FCSTD DOCUMENT  (FreeCAD 0.19R24276 (Git))
Label: redlizard
Comment: haldis 3d red lizard hotend
License: All rights reserved
LicenseURL: http://en.wikipedia.org/wiki/All_rights_reserved
objects: PartDesign::Plane×33, Sketcher::SketchObject×28, PartDesign::Pocket×24, Part::Helix×19, Part::Part2DObjectPython×15, PartDesign::ShapeBinder×15, PartDesign::Body×11, PartDesign::SubtractivePipe×11, PartDesign::Revolution×4, PartDesign::AdditivePipe×4, PartDesign::FeatureBase×4, PartDesign::Pad×3, PartDesign::SubShapeBinder×2, PartDesign::Groove×1, App::Part×1
note: 221 computed .brp shape members not serialized (recipe doc carries the construction recipe); baked Part::Feature solids carry a one-line shape summary decoded from their .brp

FEATURE [PartDesign::Plane] DatumPlane
  Length = 60
  MapMode = 2
  Placement = pos=(0,0,0) rot=(0.57735,0.57735,0.57735;4.18879rad)
  ResizeMode = 0
  Support = -> [Z_Axis001]
  Width = 60
FEATURE [Sketcher::SketchObject] Sketch
  FullyConstrained = true
  MapMode = 5
  Placement = pos=(0,0,0) rot=(0.57735,0.57735,0.57735;4.18879rad)
  Support = -> [DatumPlane]
  sketch-geometry (9):
    g0: LineSegment StartX=0 StartY=0.2 StartZ=0 EndX=0 EndY=0.5 EndZ=0
    g1: LineSegment StartX=0 StartY=0.5 StartZ=0 EndX=4 EndY=4.45 EndZ=0
    g2: LineSegment StartX=4 StartY=4.45 StartZ=0 EndX=8 EndY=4.45 EndZ=0
    g3: LineSegment StartX=8 StartY=4.45 StartZ=0 EndX=8 EndY=2.5 EndZ=0
    g4: LineSegment StartX=8 StartY=2.5 StartZ=0 EndX=9 EndY=2.5 EndZ=0
    g5: LineSegment StartX=9 StartY=2.5 StartZ=0 EndX=9 EndY=1 EndZ=0
    g6: LineSegment StartX=9 StartY=1 StartZ=0 EndX=1.64252 EndY=1 EndZ=0
    g7: LineSegment StartX=1.64252 StartY=1 StartZ=0 EndX=0.5 EndY=0.2 EndZ=0
    g8: LineSegment StartX=0.5 StartY=0.2 StartZ=0 EndX=0 EndY=0.2 EndZ=0
  constraints (27):
    c: PointOnObject(g0,g-2)
    c: PointOnObject(g0,g-2)
    c: Coincident(g0,g1)
    c: Coincident(g1,g2)
    c: Horizontal(g2)
    c: Coincident(g2,g3)
    c: Vertical(g3)
    c: Coincident(g3,g4)
    c: Horizontal(g4)
    c: Vertical(g5)
    c: Coincident(g5,g6)
    c: Coincident(g6,g7)
    c: Coincident(g7,g8)
    c: Coincident(g8,g0)
    c: Horizontal(g8)
    c: Distance(g-1,g6) = 1
    c: Horizontal(g6)
    c: Distance(g-1,g8) = 0.2
    c: Distance(g0,g-1) = 0.5
    c: Distance(g4) = 1
    c: Distance(g-1,g4) = 2.5
    c: Distance(g-1,g2) = 4.45
    c: Distance(g-1,g3) = 8
    c: Distance(g1,g-2) = 4
    c: Angle(g7,g-1) = 2.53073
    c: Distance(g8) = 0.5
    c: Coincident(g5,g4)
FEATURE [PartDesign::Revolution] Revolution
  Angle = 360
  Axis = (-4e-16,4e-16,1)
  Base = (0,0,0)
  Placement = pos=(0,0,0) rot=(0.57735,0.57735,0.57735;4.18879rad)
  Profile = -> Sketch
  ReferenceAxis = -> Sketch [H_Axis]
FEATURE [PartDesign::Plane] DatumPlane001
  Length = 60
  MapMode = 11
  Placement = pos=(0,0,-1e-16) rot=(0,0,1;1.5708rad)
  ResizeMode = 0
  Support = -> [Revolution]
  Width = 60
FEATURE [Sketcher::SketchObject] Sketch001
  FullyConstrained = true
  MapMode = 5
  Placement = pos=(0,0,-1e-16) rot=(0,0,1;1.5708rad)
  Support = -> [DatumPlane001]
  sketch-geometry (8):
    g0: LineSegment StartX=4 StartY=2.3094 StartZ=0 EndX=7.1e-15 EndY=4.6188 EndZ=0
    g1: LineSegment StartX=7.1e-15 StartY=4.6188 StartZ=0 EndX=-4 EndY=2.3094 EndZ=0
    g2: LineSegment StartX=-4 StartY=2.3094 StartZ=0 EndX=-4 EndY=-2.3094 EndZ=0
    g3: LineSegment StartX=-4 StartY=-2.3094 StartZ=0 EndX=-4.4e-15 EndY=-4.6188 EndZ=0
    g4: LineSegment StartX=-4.4e-15 StartY=-4.6188 StartZ=0 EndX=4 EndY=-2.3094 EndZ=0
    g5: LineSegment StartX=4 StartY=-2.3094 StartZ=0 EndX=4 EndY=2.3094 EndZ=0
    g6: Circle CenterX=0 CenterY=0 CenterZ=0 NormalX=0 NormalY=0 NormalZ=1 AngleXU=0 Radius=4.6188
    g7: Circle CenterX=0 CenterY=0 CenterZ=0 NormalX=0 NormalY=0 NormalZ=1 AngleXU=0 Radius=5
  constraints (18):
    c: Coincident(g0,g1)
    c: Coincident(g1,g2)
    c: Coincident(g2,g3)
    c: Coincident(g3,g4)
    c: Coincident(g4,g5)
    c: Coincident(g5,g0)
    c: Equal(g0, g1-g5) x5
    c: PointOnObject(g0,g6)
    c: PointOnObject(g1,g6)
    c: PointOnObject(g2,g6)
    c: PointOnObject(g3,g6)
    c: PointOnObject(g4,g6)
    c: PointOnObject(g5,g6)
    c: Coincident(g6,g-1)
    c: Perpendicular(g-1,g2)
    c: Distance(g3,g0) = 8
    c: Coincident(g7,g-1)
    c: Radius(g7) = 5
FEATURE [PartDesign::Pocket] Pocket
  BaseFeature = -> Revolution
  Length = 5
  Length2 = 100
  Placement = pos=(0,0,0) rot=(0.57735,0.57735,0.57735;4.18879rad)
  Profile = -> Sketch001
  Reversed = true
  Type = 1
FEATURE [PartDesign::Plane] DatumPlane003
  Length = 81.2898
  MapMode = 2
  Placement = pos=(0,0,0) rot=(0.57735,0.57735,0.57735;4.18879rad)
  ResizeMode = 0
  Support = -> [Z_Axis002]
  Width = 61.7898
FEATURE [PartDesign::Plane] DatumPlane004
  AttachmentOffset = pos=(0,0,-18.5) rot=(0,0,1;0rad)
  Length = 60
  MapMode = 5
  Placement = pos=(0,0,18.5) rot=(0,1,0;3.14159rad)
  ResizeMode = 0
  Support = -> [XY_Plane003]
  Width = 60
FEATURE [Sketcher::SketchObject] Sketch004
  FullyConstrained = true
  MapMode = 5
  Placement = pos=(0,0,18.5) rot=(0,1,0;3.14159rad)
  Support = -> [DatumPlane004]
  sketch-geometry (7):
    g0: LineSegment StartX=-10 StartY=6 StartZ=0 EndX=10 EndY=6 EndZ=0
    g1: LineSegment StartX=10 StartY=6 StartZ=0 EndX=10 EndY=-14 EndZ=0
    g2: LineSegment StartX=10 StartY=-14 StartZ=0 EndX=-10 EndY=-14 EndZ=0
    g3: LineSegment StartX=-10 StartY=-14 StartZ=0 EndX=-10 EndY=6 EndZ=0
    g4: Circle CenterX=-8 CenterY=0 CenterZ=0 NormalX=0 NormalY=0 NormalZ=1 AngleXU=0 Radius=0.8
    g5: Circle CenterX=8 CenterY=0 CenterZ=0 NormalX=0 NormalY=0 NormalZ=1 AngleXU=0 Radius=0.8
    g6: Circle CenterX=0 CenterY=0 CenterZ=0 NormalX=0 NormalY=0 NormalZ=1 AngleXU=0 Radius=2.3
  constraints (18):
    c: Coincident(g0,g1)
    c: Coincident(g1,g2)
    c: Coincident(g2,g3)
    c: Coincident(g3,g0)
    c: Horizontal(g2)
    c: Vertical(g1)
    c: Vertical(g3)
    c: Equal(g0,g1)
    c: Symmetric(g0,g0,g-2)
    c: Distance(g0,g-1) = 6
    c: Distance(g0) = 20
    c: PointOnObject(g4,g-1)
    c: Equal(g4,g5)
    c: Symmetric(g5,g4,g-1)
    c: Radius(g5) = 0.8
    c: Distance(g5,g4) = 16
    c: Coincident(g6,g-1)
    c: Radius(g6) = 2.3
FEATURE [PartDesign::Pad] Pad
  Direction = (1,1,1)
  Length = 10
  Length2 = 100
  Placement = pos=(0,0,18.5) rot=(0,1,0;3.14159rad)
  Profile = -> Sketch004
  Type = 0
FEATURE [PartDesign::Plane] DatumPlane005
  Length = 60
  MapMode = 5
  Placement = pos=(10,0,18.5) rot=(0.57735,-0.57735,0.57735;4.18879rad)
  ResizeMode = 0
  Support = -> [Pad]
  Width = 60
FEATURE [Sketcher::SketchObject] Sketch005
  FullyConstrained = true
  MapMode = 5
  Placement = pos=(10,0,18.5) rot=(-0.57735,0.57735,-0.57735;2.0944rad)
  Support = -> [DatumPlane005]
  sketch-geometry (6):
    g0: Circle CenterX=9.9 CenterY=5.5 CenterZ=0 NormalX=0 NormalY=0 NormalZ=1 AngleXU=0 Radius=3.1
    g1: Circle CenterX=6 CenterY=2.2 CenterZ=0 NormalX=0 NormalY=0 NormalZ=1 AngleXU=0 Radius=1.55
    g2: Circle CenterX=3 CenterY=4.5 CenterZ=0 NormalX=0 NormalY=0 NormalZ=1 AngleXU=0 Radius=1.18
    g3: Circle CenterX=3 CenterY=8 CenterZ=0 NormalX=0 NormalY=0 NormalZ=1 AngleXU=0 Radius=1
    g4: LineSegment StartX=3 StartY=10 StartZ=0 EndX=3 EndY=6 EndZ=0
    g5: Circle CenterX=3 CenterY=4.5 CenterZ=0 NormalX=0 NormalY=0 NormalZ=1 AngleXU=0 Radius=1.5
  constraints (17):
    c: Radius(g0) = 3.1
    c: Radius(g3) = 1
    c: Radius(g2) = 1.18
    c: Radius(g1) = 1.55
    c: Distance(g1,g-1) = 2.2
    c: Distance(g2,g-1) = 4.5
    c: Vertical(g3,g2)
    c: Vertical(g4)
    c: Symmetric(g4,g4,g3)
    c: Coincident(g5,g2)
    c: Radius(g5) = 1.5
    c: PointOnObject(g4,g5)
    c: DistanceX(g0) = 9.9
    c: DistanceY(g0) = 5.5
    c: DistanceX(g1) = 6
    c: DistanceX(g2) = 3
    c: DistanceY(g4) = 10
FEATURE [PartDesign::Pocket] Pocket002
  BaseFeature = -> Pad
  Length = 5
  Length2 = 100
  Placement = pos=(0,0,18.5) rot=(0,1,0;3.14159rad)
  Profile = -> Sketch005
  Type = 0
FEATURE [PartDesign::Plane] DatumPlane006
  Length = 60
  MapMode = 5
  Placement = pos=(0,0,18.5) rot=(0,0,1;3.14159rad)
  ResizeMode = 0
  Support = -> [Pocket002]
  Width = 60
FEATURE [Sketcher::SketchObject] Sketch006
  FullyConstrained = true
  MapMode = 5
  Placement = pos=(0,0,18.5) rot=(0,0,1;3.14159rad)
  Support = -> [DatumPlane006]
  sketch-geometry (1):
    g0: Circle CenterX=0 CenterY=9.9 CenterZ=0 NormalX=0 NormalY=0 NormalZ=1 AngleXU=0 Radius=1.18
  constraints (3):
    c: PointOnObject(g0,g-2)
    c: Radius(g0) = 1.18
    c: Distance(g0,g-1) = 9.9
FEATURE [PartDesign::Pocket] Pocket006
  BaseFeature = -> Pocket002
  Length = 5
  Length2 = 100
  Placement = pos=(0,0,18.5) rot=(0,1,0;3.14159rad)
  Profile = -> Sketch006
  Type = 0
FEATURE [PartDesign::Plane] DatumPlane007
  Length = 60
  MapMode = 5
  Placement = pos=(-3.7e-15,0,8.5) rot=(0,1,0;3.14159rad)
  ResizeMode = 0
  Support = -> [Pocket006]
  Width = 60
FEATURE [Sketcher::SketchObject] Sketch007
  FullyConstrained = true
  MapMode = 5
  Placement = pos=(-3.7e-15,0,8.5) rot=(0,1,0;3.14159rad)
  Support = -> [DatumPlane007]
  sketch-geometry (1):
    g0: Circle CenterX=4 CenterY=-5 CenterZ=0 NormalX=0 NormalY=0 NormalZ=1 AngleXU=0 Radius=1.18
  constraints (3):
    c: Radius(g0) = 1.18
    c: Distance(g0,g-2) = 4
    c: Distance(g0,g-1) = 5
FEATURE [PartDesign::Pocket] Pocket007
  BaseFeature = -> Pocket006
  Length = 7
  Length2 = 100
  Placement = pos=(0,0,18.5) rot=(0,1,0;3.14159rad)
  Profile = -> Sketch007
  Type = 0
FEATURE [Sketcher::SketchObject] Sketch008
  ExternalGeometry = -> [Pocket007]
  FullyConstrained = true
  MapMode = 5
  Placement = pos=(0,0,18.5) rot=(0,1,0;3.14159rad)
  Support = -> [DatumPlane004]
  sketch-geometry (4):
    g0: Circle CenterX=-6 CenterY=3 CenterZ=0 NormalX=0 NormalY=0 NormalZ=1 AngleXU=0 Radius=1
    g1: Circle CenterX=-6 CenterY=-3 CenterZ=0 NormalX=0 NormalY=0 NormalZ=1 AngleXU=0 Radius=1
    g2: Circle CenterX=6 CenterY=3 CenterZ=0 NormalX=0 NormalY=0 NormalZ=1 AngleXU=0 Radius=1
    g3: Circle CenterX=6 CenterY=-3 CenterZ=0 NormalX=0 NormalY=0 NormalZ=1 AngleXU=0 Radius=1
  constraints (10):
    c: Equal(g3,g2)
    c: Equal(g2,g0)
    c: Equal(g0,g1)
    c: Horizontal(g1,g3)
    c: Vertical(g2,g3)
    c: Symmetric(g0,g2,g-2)
    c: Symmetric(g1,g0,g-1)
    c: Distance(g0,g1) = 6
    c: Distance(g2,g0) = 12
    c: Radius(g2) = 1
FEATURE [PartDesign::Pocket] Pocket008
  BaseFeature = -> Pocket007
  Length = 2.5
  Length2 = 100
  Placement = pos=(0,0,18.5) rot=(0,1,0;3.14159rad)
  Profile = -> Sketch008
  Reversed = true
  Type = 0
FEATURE [PartDesign::Plane] DatumPlane010
  Length = 93.1886
  MapMode = 2
  Placement = pos=(0,0,0) rot=(0.57735,0.57735,0.57735;4.18879rad)
  ResizeMode = 0
  Support = -> [Z_Axis004]
  Width = 62.6886
FEATURE [Sketcher::SketchObject] Sketch009
  FullyConstrained = true
  MapMode = 5
  Placement = pos=(0,0,0) rot=(0.57735,0.57735,0.57735;4.18879rad)
  Support = -> [DatumPlane010]
  sketch-geometry (71):
    g0: LineSegment StartX=23.5 StartY=0 StartZ=0 EndX=23.5 EndY=10.5 EndZ=0
    g1: LineSegment StartX=55.5 StartY=10.5 StartZ=0 EndX=55.5 EndY=0 EndZ=0
    g2: LineSegment StartX=55.5 StartY=0 StartZ=0 EndX=23.5 EndY=0 EndZ=0
    g3: LineSegment StartX=23.5 StartY=10.5 StartZ=0 EndX=26.5 EndY=10.5 EndZ=0
    g4: LineSegment StartX=55.5 StartY=10.5 StartZ=0 EndX=43.5 EndY=10.5 EndZ=0
    g5: LineSegment StartX=23.5 StartY=8.5 StartZ=0 EndX=55.5 EndY=8.5 EndZ=0
    g6: LineSegment StartX=23.5 StartY=8.3 StartZ=0 EndX=55.5 EndY=8.3 EndZ=0
    g7: LineSegment StartX=26.5 StartY=10.5 StartZ=0 EndX=26.5 EndY=8.5 EndZ=0
    g8: LineSegment StartX=26.5 StartY=8.5 StartZ=0 EndX=27.5 EndY=8.5 EndZ=0
    g9: LineSegment StartX=43.5 StartY=10.5 StartZ=0 EndX=43.5 EndY=8.5 EndZ=0
    g10: LineSegment StartX=43.5 StartY=8.5 StartZ=0 EndX=42.5 EndY=8.5 EndZ=0
    g11: LineSegment StartX=27.5 StartY=8.5 StartZ=0 EndX=27.5 EndY=10.5 EndZ=0
    g12: LineSegment StartX=27.5 StartY=10.5 StartZ=0 EndX=28.2778 EndY=10.5 EndZ=0
    g13: LineSegment StartX=28.2778 StartY=10.5 StartZ=0 EndX=28.2778 EndY=7.3 EndZ=0
    g14: LineSegment StartX=28.2778 StartY=7.3 StartZ=0 EndX=29.2778 EndY=7.3 EndZ=0
    g15: LineSegment StartX=29.2778 StartY=7.3 StartZ=0 EndX=29.2778 EndY=10.5 EndZ=0
    g16: LineSegment StartX=29.2778 StartY=10.5 StartZ=0 EndX=30.0556 EndY=10.5 EndZ=0
    g17: LineSegment StartX=30.0556 StartY=10.5 StartZ=0 EndX=30.0556 EndY=7.3 EndZ=0
    g18: LineSegment StartX=30.0556 StartY=7.3 StartZ=0 EndX=31.0556 EndY=7.3 EndZ=0
    g19: LineSegment StartX=31.0556 StartY=7.3 StartZ=0 EndX=31.0556 EndY=10.5 EndZ=0
    g20: LineSegment StartX=31.0556 StartY=10.5 StartZ=0 EndX=31.8333 EndY=10.5 EndZ=0
    g21: LineSegment StartX=31.8333 StartY=10.5 StartZ=0 EndX=31.8333 EndY=7.3 EndZ=0
    g22: LineSegment StartX=31.8333 StartY=7.3 StartZ=0 EndX=32.8333 EndY=7.3 EndZ=0
    g23: LineSegment StartX=32.8333 StartY=7.3 StartZ=0 EndX=32.8333 EndY=10.5 EndZ=0
    g24: LineSegment StartX=32.8333 StartY=10.5 StartZ=0 EndX=33.6111 EndY=10.5 EndZ=0
    g25: LineSegment StartX=33.6111 StartY=10.5 StartZ=0 EndX=33.6111 EndY=7.3 EndZ=0
    g26: LineSegment StartX=33.6111 StartY=7.3 StartZ=0 EndX=34.6111 EndY=7.3 EndZ=0
    g27: LineSegment StartX=34.6111 StartY=7.3 StartZ=0 EndX=34.6111 EndY=10.5 EndZ=0
    g28: LineSegment StartX=34.6111 StartY=10.5 StartZ=0 EndX=35.3889 EndY=10.5 EndZ=0
    g29: LineSegment StartX=35.3889 StartY=10.5 StartZ=0 EndX=35.3889 EndY=7.3 EndZ=0
    g30: LineSegment StartX=35.3889 StartY=7.3 StartZ=0 EndX=36.3889 EndY=7.3 EndZ=0
    g31: LineSegment StartX=36.3889 StartY=7.3 StartZ=0 EndX=36.3889 EndY=10.5 EndZ=0
    g32: LineSegment StartX=36.3889 StartY=10.5 StartZ=0 EndX=37.1667 EndY=10.5 EndZ=0
    g33: LineSegment StartX=37.1667 StartY=10.5 StartZ=0 EndX=37.1667 EndY=7.3 EndZ=0
    g34: LineSegment StartX=37.1667 StartY=7.3 StartZ=0 EndX=38.1667 EndY=7.3 EndZ=0
    g35: LineSegment StartX=38.1667 StartY=7.3 StartZ=0 EndX=38.1667 EndY=10.5 EndZ=0
    g36: LineSegment StartX=38.1667 StartY=10.5 StartZ=0 EndX=38.9444 EndY=10.5 EndZ=0
    g37: LineSegment StartX=38.9444 StartY=10.5 StartZ=0 EndX=38.9444 EndY=7.3 EndZ=0
    g38: LineSegment StartX=38.9444 StartY=7.3 StartZ=0 EndX=39.9444 EndY=7.3 EndZ=0
    g39: LineSegment StartX=39.9444 StartY=7.3 StartZ=0 EndX=39.9444 EndY=10.5 EndZ=0
    g40: LineSegment StartX=39.9444 StartY=10.5 StartZ=0 EndX=40.7222 EndY=10.5 EndZ=0
    g41: LineSegment StartX=40.7222 StartY=10.5 StartZ=0 EndX=40.7222 EndY=7.3 EndZ=0
    g42: LineSegment StartX=40.7222 StartY=7.3 StartZ=0 EndX=41.7222 EndY=7.3 EndZ=0
    g43: LineSegment StartX=41.7222 StartY=7.3 StartZ=0 EndX=41.7222 EndY=10.5 EndZ=0
    g44: LineSegment StartX=41.7222 StartY=10.5 StartZ=0 EndX=42.5 EndY=10.5 EndZ=0
    g45: LineSegment StartX=42.5 StartY=10.5 StartZ=0 EndX=42.5 EndY=8.5 EndZ=0
    g46: ArcOfCircle CenterX=35 CenterY=121.371 CenterZ=0 NormalX=0 NormalY=0 NormalZ=1 AngleXU=0 Radius=113.071 StartAngle=4.6529 EndAngle=4.77188
    g47: ArcOfCircle CenterX=35 CenterY=121.371 CenterZ=0 NormalX=0 NormalY=0 NormalZ=1 AngleXU=0 Radius=113.071 StartAngle=4.6529 EndAngle=4.66176
    g48: LineSegment StartX=28.2778 StartY=10.5 StartZ=0 EndX=28.2778 EndY=8.5 EndZ=0
    g49: LineSegment StartX=29.2778 StartY=10.5 StartZ=0 EndX=29.2778 EndY=8.44489 EndZ=0
    g50: LineSegment StartX=30.0556 StartY=10.5 StartZ=0 EndX=30.0556 EndY=8.40816 EndZ=0
    g51: LineSegment StartX=31.0556 StartY=10.5 StartZ=0 EndX=31.0556 EndY=8.36882 EndZ=0
    g52: LineSegment StartX=31.8333 StartY=10.5 StartZ=0 EndX=31.8333 EndY=8.34435 EndZ=0
    g53: LineSegment StartX=32.8333 StartY=10.5 StartZ=0 EndX=32.8333 EndY=8.32076 EndZ=0
    g54: LineSegment StartX=33.6111 StartY=10.5 StartZ=0 EndX=33.6111 EndY=8.30853 EndZ=0
    g55: LineSegment StartX=34.6111 StartY=10.5 StartZ=0 EndX=34.6111 EndY=8.30067 EndZ=0
    g56: LineSegment StartX=35.3889 StartY=10.5 StartZ=0 EndX=35.3889 EndY=8.30067 EndZ=0
    g57: LineSegment StartX=36.3889 StartY=10.5 StartZ=0 EndX=36.3889 EndY=8.30853 EndZ=0
    g58: LineSegment StartX=37.1667 StartY=10.5 StartZ=0 EndX=37.1667 EndY=8.32076 EndZ=0
    g59: LineSegment StartX=38.1667 StartY=10.5 StartZ=0 EndX=38.1667 EndY=8.34435 EndZ=0
    g60: LineSegment StartX=38.9444 StartY=10.5 StartZ=0 EndX=38.9444 EndY=8.36882 EndZ=0
    g61: LineSegment StartX=39.9444 StartY=10.5 StartZ=0 EndX=39.9444 EndY=8.40816 EndZ=0
    g62: LineSegment StartX=40.7222 StartY=10.5 StartZ=0 EndX=40.7222 EndY=8.44489 EndZ=0
    g63: LineSegment StartX=41.7222 StartY=10.5 StartZ=0 EndX=41.7222 EndY=8.5 EndZ=0
    g64: ArcOfCircle CenterX=35 CenterY=121.371 CenterZ=0 NormalX=0 NormalY=0 NormalZ=1 AngleXU=0 Radius=113.071 StartAngle=4.76302 EndAngle=4.77188
    g65: ArcOfCircle CenterX=35 CenterY=121.371 CenterZ=0 NormalX=0 NormalY=0 NormalZ=1 AngleXU=0 Radius=113.071 StartAngle=4.74728 EndAngle=4.75613
    g66: ArcOfCircle CenterX=35 CenterY=121.371 CenterZ=0 NormalX=0 NormalY=0 NormalZ=1 AngleXU=0 Radius=113.071 StartAngle=4.73155 EndAngle=4.7404
    g67: ArcOfCircle CenterX=35 CenterY=121.371 CenterZ=0 NormalX=0 NormalY=0 NormalZ=1 AngleXU=0 Radius=113.071 StartAngle=4.71583 EndAngle=4.72467
    g68: ArcOfCircle CenterX=35 CenterY=121.371 CenterZ=0 NormalX=0 NormalY=0 NormalZ=1 AngleXU=0 Radius=113.071 StartAngle=4.70011 EndAngle=4.70895
    g69: ArcOfCircle CenterX=35 CenterY=121.371 CenterZ=0 NormalX=0 NormalY=0 NormalZ=1 AngleXU=0 Radius=113.071 StartAngle=4.68438 EndAngle=4.69323
    g70: ArcOfCircle CenterX=35 CenterY=121.371 CenterZ=0 NormalX=0 NormalY=0 NormalZ=1 AngleXU=0 Radius=113.071 StartAngle=4.66865 EndAngle=4.6775
  constraints (222):
    c: PointOnObject(g0,g-1)
    c: Vertical(g0)
    c: PointOnObject(g1,g-1)
    c: Vertical(g1)
    c: Coincident(g1,g2)
    c: Coincident(g2,g0)
    c: Distance(g1) = 10.5
    c: Distance(g2) = 32
    c: Coincident(g3,g0)
    c: Horizontal(g3)
    c: Coincident(g4,g1)
    c: Horizontal(g4)
    c: Distance(g4) = 12
    c: Distance(g3) = 3
    c: Horizontal(g0,g1)
    c: PointOnObject(g5,g1)
    c: Horizontal(g5)
    c: PointOnObject(g5,g0)
    c: Distance(g3,g5) = 2
    c: PointOnObject(g6,g0)
    c: PointOnObject(g6,g1)
    c: Horizontal(g6)
    c: Distance(g3,g6) = 2.2
    c: Coincident(g7,g3)
    c: PointOnObject(g7,g5)
    c: Vertical(g7)
    c: Coincident(g8,g7)
    c: PointOnObject(g8,g5)
    c: Coincident(g9,g4)
    c: PointOnObject(g9,g5)
    c: Vertical(g9)
    c: Coincident(g10,g9)
    c: PointOnObject(g10,g5)
    c: Equal(g8,g10)
    c: Distance(g8) = 1
    c: Coincident(g8,g11)
    c: Vertical(g11)
    c: Coincident(g11,g12)
    c: Horizontal(g12)
    c: Coincident(g12,g13)
    c: Vertical(g13)
    c: Coincident(g13,g14)
    c: Horizontal(g14)
    c: Coincident(g14,g15)
    c: Vertical(g15)
    c: Coincident(g15,g16)
    c: Horizontal(g16)
    c: Coincident(g16,g17)
    c: Vertical(g17)
    c: Coincident(g17,g18)
    c: Horizontal(g18)
    c: Coincident(g18,g19)
    c: Vertical(g19)
    c: Coincident(g19,g20)
    c: Horizontal(g20)
    c: Coincident(g20,g21)
    c: Vertical(g21)
    c: Coincident(g21,g22)
    c: Horizontal(g22)
    c: Coincident(g22,g23)
    c: Vertical(g23)
    c: Coincident(g23,g24)
    c: Horizontal(g24)
    c: Coincident(g24,g25)
    c: Vertical(g25)
    c: Coincident(g25,g26)
    c: Horizontal(g26)
    c: Coincident(g26,g27)
    c: Vertical(g27)
    c: Coincident(g27,g28)
    c: Horizontal(g28)
    c: Coincident(g28,g29)
    c: Vertical(g29)
    c: Coincident(g29,g30)
    c: Horizontal(g30)
    c: Coincident(g30,g31)
    c: Vertical(g31)
    c: Coincident(g31,g32)
    c: Horizontal(g32)
    c: Coincident(g32,g33)
    c: Vertical(g33)
    c: Coincident(g33,g34)
    c: Horizontal(g34)
    c: Coincident(g34,g35)
    c: Vertical(g35)
    c: Coincident(g35,g36)
    c: Horizontal(g36)
    c: Coincident(g36,g37)
    c: Vertical(g37)
    c: Coincident(g37,g38)
    c: Horizontal(g38)
    c: Coincident(g38,g39)
    c: Vertical(g39)
    c: Coincident(g39,g40)
    c: Horizontal(g40)
    c: Coincident(g40,g41)
    c: Vertical(g41)
    c: Coincident(g41,g42)
    c: Horizontal(g42)
    c: Coincident(g42,g43)
    c: Vertical(g43)
    c: Coincident(g43,g44)
    c: Horizontal(g44)
    c: Coincident(g44,g45)
    c: Coincident(g45,g10)
    c: Vertical(g45)
    c: Horizontal(g3,g12)
    c: Horizontal(g12,g16)
    c: Horizontal(g16,g20)
    c: Horizontal(g20,g24)
    c: Horizontal(g24,g28)
    c: Horizontal(g28,g32)
    c: Horizontal(g32,g36)
    c: Horizontal(g36,g40)
    c: Horizontal(g40,g44)
    c: Equal(g8,g14)
    c: Equal(g14,g18)
    c: Equal(g18,g22)
    c: Equal(g22,g26)
    c: Equal(g26,g30)
    c: Equal(g30,g34)
    c: Equal(g34,g38)
    c: Equal(g38,g42)
    c: Equal(g12,g16)
    c: Equal(g16,g20)
    c: Equal(g20,g24)
    c: Equal(g24,g28)
    c: Equal(g28,g32)
    c: Equal(g32,g36)
    c: Equal(g36,g40)
    c: Equal(g40,g44)
    c: PointOnObject(g46,g13)
    c: PointOnObject(g46,g43)
    c: PointOnObject(g46,g5)
    c: PointOnObject(g46,g5)
    c: Tangent(g46,g6)
    c: Coincident(g47,g46)
    c: Coincident(g47,g46)
    c: Coincident(g64,g46)
    c: Coincident(g48,g12)
    c: Coincident(g48,g47)
    c: Vertical(g48)
    c: Coincident(g49,g16)
    c: PointOnObject(g49,g47)
    c: Vertical(g49)
    c: Coincident(g50,g16)
    c: PointOnObject(g50,g47)
    c: Vertical(g50)
    c: Coincident(g51,g20)
    c: PointOnObject(g51,g47)
    c: Vertical(g51)
    c: Coincident(g52,g20)
    c: PointOnObject(g52,g47)
    c: Vertical(g52)
    c: Coincident(g53,g24)
    c: PointOnObject(g53,g47)
    c: Vertical(g53)
    c: Coincident(g54,g24)
    c: PointOnObject(g54,g47)
    c: Vertical(g54)
    c: Coincident(g55,g28)
    c: PointOnObject(g55,g47)
    c: Vertical(g55)
    c: Coincident(g56,g28)
    c: PointOnObject(g56,g47)
    c: Vertical(g56)
    c: Coincident(g57,g32)
    c: PointOnObject(g57,g47)
    c: Vertical(g57)
    c: Coincident(g58,g32)
    c: PointOnObject(g58,g47)
    c: Vertical(g58)
    c: Coincident(g59,g36)
    c: Vertical(g59)
    c: Coincident(g60,g36)
    c: PointOnObject(g60,g47)
    c: Vertical(g60)
    c: Coincident(g61,g40)
    c: PointOnObject(g61,g47)
    c: Vertical(g61)
    c: Coincident(g62,g40)
    c: PointOnObject(g62,g47)
    c: Vertical(g62)
    c: Coincident(g63,g44)
    c: PointOnObject(g63,g47)
    c: Vertical(g63)
    c: Equal(g47,g64)
    c: PointOnObject(g65,g39)
    c: PointOnObject(g64,g41)
    c: Coincident(g47,g64)
    c: Equal(g47,g65)
    c: Coincident(g66,g59)
    c: PointOnObject(g65,g37)
    c: Coincident(g47,g65)
    c: Equal(g47,g66)
    c: PointOnObject(g67,g31)
    c: PointOnObject(g66,g33)
    c: Coincident(g47,g66)
    c: PointOnObject(g68,g27)
    c: Coincident(g47,g67)
    c: Equal(g47,g68)
    c: PointOnObject(g69,g23)
    c: PointOnObject(g68,g25)
    c: Coincident(g47,g68)
    c: Equal(g47,g69)
    c: PointOnObject(g70,g19)
    c: PointOnObject(g69,g21)
    c: Coincident(g47,g69)
    c: Equal(g47,g70)
    c: PointOnObject(g47,g15)
    c: PointOnObject(g70,g17)
    c: Coincident(g47,g70)
    c: Coincident(g67,g56)
    c: Horizontal(g14,g18)
    c: Horizontal(g18,g22)
    c: Horizontal(g22,g26)
    c: Horizontal(g26,g30)
    c: Horizontal(g30,g34)
    c: Horizontal(g34,g38)
    c: Horizontal(g38,g42)
    c: Distance(g42,g6) = 1
    c: Distance(g0,g-2) = 23.5
FEATURE [PartDesign::Revolution] Revolution002
  Angle = 360
  Axis = (-4e-16,4e-16,1)
  Base = (0,0,0)
  Placement = pos=(0,0,0) rot=(0.57735,0.57735,0.57735;4.18879rad)
  Profile = -> Sketch009
  ReferenceAxis = -> Sketch009 [H_Axis]
FEATURE [PartDesign::Plane] DatumPlane011
  Length = 62.6886
  MapMode = 5
  Placement = pos=(0,0,0) rot=(0.57735,0.57735,0.57735;2.0944rad)
  ResizeMode = 0
  Support = -> [YZ_Plane004]
  Width = 93.1886
FEATURE [Sketcher::SketchObject] Sketch010
  ExternalGeometry = -> [Revolution002]
  FullyConstrained = true
  MapMode = 5
  Placement = pos=(0,0,0) rot=(0.57735,0.57735,0.57735;2.0944rad)
  Support = -> [DatumPlane011]
  sketch-geometry (9):
    g0: LineSegment StartX=-6 StartY=55.5 StartZ=0 EndX=6 EndY=55.5 EndZ=0
    g1: LineSegment StartX=6 StartY=55.5 StartZ=0 EndX=6 EndY=23.5 EndZ=0
    g2: LineSegment StartX=6 StartY=23.5 StartZ=0 EndX=-6 EndY=23.5 EndZ=0
    g3: LineSegment StartX=-6 StartY=23.5 StartZ=0 EndX=-6 EndY=55.5 EndZ=0
    g4: LineSegment StartX=-12.5 StartY=58.5476 StartZ=0 EndX=12.5 EndY=58.5476 EndZ=0
    g5: LineSegment StartX=12.5 StartY=58.5476 StartZ=0 EndX=12.5 EndY=20.4524 EndZ=0
    g6: LineSegment StartX=12.5 StartY=20.4524 StartZ=0 EndX=-12.5 EndY=20.4524 EndZ=0
    g7: LineSegment StartX=-12.5 StartY=20.4524 StartZ=0 EndX=-12.5 EndY=58.5476 EndZ=0
    g8: LineSegment StartX=12.5 StartY=58.5476 StartZ=0 EndX=-12.5 EndY=20.4524 EndZ=0
  constraints (24):
    c: Coincident(g0,g1)
    c: Coincident(g1,g2)
    c: Coincident(g2,g3)
    c: Coincident(g3,g0)
    c: Horizontal(g2)
    c: Vertical(g1)
    c: Vertical(g3)
    c: PointOnObject(g0,g-3)
    c: PointOnObject(g1,g-4)
    c: Symmetric(g0,g0,g-2)
    c: Distance(g0) = 12
    c: Coincident(g4,g5)
    c: Coincident(g5,g6)
    c: Coincident(g6,g7)
    c: Coincident(g7,g4)
    c: Horizontal(g6)
    c: Vertical(g5)
    c: Vertical(g7)
    c: Symmetric(g4,g4,g-2)
    c: Distance(g6) = 25
    c: Coincident(g8,g4)
    c: Coincident(g8,g6)
    c: PointOnObject(g-4,g8)
    c: PointOnObject(g-3,g8)
FEATURE [PartDesign::Pocket] Pocket010
  BaseFeature = -> Revolution002
  Length = 5
  Length2 = 100
  Midplane = true
  Placement = pos=(0,0,0) rot=(0.57735,0.57735,0.57735;4.18879rad)
  Profile = -> Sketch010
  Type = 1
FEATURE [PartDesign::Plane] DatumPlane012
  Length = 62.6886
  MapMode = 5
  Placement = pos=(0,0,0) rot=(1,0,0;1.5708rad)
  ResizeMode = 0
  Support = -> [XZ_Plane004]
  Width = 93.1886
FEATURE [Sketcher::SketchObject] Sketch011
  ExternalGeometry = -> [Pocket010]
  FullyConstrained = true
  MapMode = 5
  Placement = pos=(0,0,0) rot=(1,0,0;1.5708rad)
  Support = -> [DatumPlane012]
  sketch-geometry (8):
    g0: LineSegment StartX=-5.25 StartY=42.5 StartZ=0 EndX=5.25 EndY=42.5 EndZ=0
    g1: LineSegment StartX=6.25 StartY=41.5 StartZ=0 EndX=6.25 EndY=27.5 EndZ=0
    g2: LineSegment StartX=5.25 StartY=26.5 StartZ=0 EndX=-5.25 EndY=26.5 EndZ=0
    g3: LineSegment StartX=-6.25 StartY=27.5 StartZ=0 EndX=-6.25 EndY=41.5 EndZ=0
    g4: ArcOfCircle CenterX=-5.25 CenterY=41.5 CenterZ=0 NormalX=0 NormalY=0 NormalZ=1 AngleXU=0 Radius=1 StartAngle=1.5708 EndAngle=3.14159
    g5: ArcOfCircle CenterX=5.25 CenterY=41.5 CenterZ=0 NormalX=0 NormalY=0 NormalZ=1 AngleXU=0 Radius=1 StartAngle=-9e-16 EndAngle=1.5708
    g6: ArcOfCircle CenterX=5.25 CenterY=27.5 CenterZ=0 NormalX=0 NormalY=0 NormalZ=1 AngleXU=0 Radius=1 StartAngle=4.71239 EndAngle=6.28319
    g7: ArcOfCircle CenterX=-5.25 CenterY=27.5 CenterZ=0 NormalX=0 NormalY=0 NormalZ=1 AngleXU=0 Radius=1 StartAngle=3.14159 EndAngle=4.71239
  constraints (19):
    c: Horizontal(g0)
    c: Horizontal(g2)
    c: Vertical(g1)
    c: Vertical(g3)
    c: Tangent(g3,g4) = 1.5708
    c: Tangent(g0,g4) = 1.5708
    c: Tangent(g0,g5) = 1.5708
    c: Tangent(g1,g5) = 1.5708
    c: Tangent(g1,g6) = 1.5708
    c: Tangent(g2,g6) = 1.5708
    c: Tangent(g2,g7) = 1.5708
    c: Tangent(g3,g7) = 1.5708
    c: Radius(g6) = 1
    c: Equal(g6,g7)
    c: Equal(g6,g4)
    c: Distance(g3,g1) = 12.5
    c: Distance(g0,g2) = 16
    c: Symmetric(g5,g4,g-2)
    c: Distance(g-1,g2) = 26.5
FEATURE [PartDesign::Pocket] Pocket011
  BaseFeature = -> Pocket010
  Length = 5
  Length2 = 100
  Midplane = true
  Placement = pos=(0,0,0) rot=(0.57735,0.57735,0.57735;4.18879rad)
  Profile = -> Sketch011
  Type = 1
FEATURE [PartDesign::Plane] DatumPlane013
  Length = 62.6886
  MapMode = 5
  Placement = pos=(0,0,0) rot=(0.57735,0.57735,0.57735;2.0944rad)
  ResizeMode = 0
  Support = -> [YZ_Plane004]
  Width = 93.1886
FEATURE [Sketcher::SketchObject] Sketch012
  ExternalGeometry = -> [Pocket011]
  FullyConstrained = true
  MapMode = 5
  Placement = pos=(0,0,0) rot=(0.57735,0.57735,0.57735;2.0944rad)
  Support = -> [DatumPlane013]
  sketch-geometry (6):
    g0: ArcOfCircle CenterX=0 CenterY=39 CenterZ=0 NormalX=0 NormalY=0 NormalZ=1 AngleXU=0 Radius=2.5 StartAngle=-9e-16 EndAngle=3.14159
    g1: ArcOfCircle CenterX=1e-16 CenterY=31 CenterZ=0 NormalX=0 NormalY=0 NormalZ=1 AngleXU=0 Radius=2.5 StartAngle=3.14159 EndAngle=6.28319
    g2: LineSegment StartX=-2.5 StartY=39 StartZ=0 EndX=-2.5 EndY=31 EndZ=0
    g3: LineSegment StartX=2.5 StartY=39 StartZ=0 EndX=2.5 EndY=31 EndZ=0
    g4: LineSegment StartX=0 StartY=41.7222 StartZ=0 EndX=0 EndY=28.2778 EndZ=0
    g5: LineSegment StartX=-2.5 StartY=35 StartZ=0 EndX=2.5 EndY=35 EndZ=0
  constraints (16):
    c: Tangent(g0,g3) = 1.5708
    c: Tangent(g0,g2) = -1.5708
    c: Tangent(g2,g1) = -1.5708
    c: Tangent(g3,g1) = 1.5708
    c: Vertical(g2)
    c: Equal(g0,g1)
    c: Radius(g0) = 2.5
    c: Distance(g0,g1) = 8
    c: PointOnObject(g0,g-2)
    c: Vertical(g4)
    c: PointOnObject(g4,g-2)
    c: PointOnObject(g5,g2)
    c: Symmetric(g0,g1,g5)
    c: Symmetric(g4,g4,g5)
    c: PointOnObject(g4,g-4)
    c: PointOnObject(g4,g-3)
FEATURE [PartDesign::Pocket] Pocket012
  BaseFeature = -> Pocket011
  Length = 5
  Length2 = 100
  Midplane = true
  Placement = pos=(0,0,0) rot=(0.57735,0.57735,0.57735;4.18879rad)
  Profile = -> Sketch012
  Type = 1
FEATURE [PartDesign::Plane] DatumPlane014
  Length = 60
  MapMode = 5
  Placement = pos=(5.9e-15,-1.47e-14,26.5) rot=(0,0,1;0rad)
  ResizeMode = 0
  Support = -> [Pocket012]
  Width = 60
FEATURE [Sketcher::SketchObject] Sketch013
  FullyConstrained = true
  MapMode = 5
  Placement = pos=(5.9e-15,-1.47e-14,26.5) rot=(0,0,1;0rad)
  Support = -> [DatumPlane014]
  sketch-geometry (1):
    g0: Circle CenterX=0 CenterY=0 CenterZ=0 NormalX=0 NormalY=0 NormalZ=1 AngleXU=0 Radius=5
  constraints (2):
    c: Coincident(g0,g-1)
    c: Radius(g0) = 5
FEATURE [PartDesign::Plane] DatumPlane015
  Length = 60
  MapMode = 5
  Placement = pos=(9.4e-15,-2.36e-14,42.5) rot=(0,1,0;3.14159rad)
  ResizeMode = 0
  Support = -> [Pocket012]
  Width = 60
FEATURE [Sketcher::SketchObject] Sketch014
  FullyConstrained = true
  MapMode = 5
  Placement = pos=(9.4e-15,-2.36e-14,42.5) rot=(0,1,0;3.14159rad)
  Support = -> [DatumPlane015]
  sketch-geometry (1):
    g0: Circle CenterX=0 CenterY=0 CenterZ=0 NormalX=0 NormalY=0 NormalZ=1 AngleXU=0 Radius=1.11
  constraints (2):
    c: Coincident(g0,g-1)
    c: Radius(g0) = 1.11
FEATURE [PartDesign::Pocket] Pocket014
  BaseFeature = -> Pocket012
  Length = 5
  Length2 = 100
  Placement = pos=(0,0,0) rot=(0.57735,0.57735,0.57735;4.18879rad)
  Profile = -> Sketch014
  Type = 1
FEATURE [Sketcher::SketchObject] Sketch015
  ExternalGeometry = -> [Pocket014]
  FullyConstrained = true
  MapMode = 5
  Placement = pos=(0,0,0) rot=(1,0,0;1.5708rad)
  Support = -> [DatumPlane012]
  sketch-geometry (2):
    g0: Circle CenterX=-7 CenterY=47.5 CenterZ=0 NormalX=0 NormalY=0 NormalZ=1 AngleXU=0 Radius=1.6
    g1: Circle CenterX=7 CenterY=47.5 CenterZ=0 NormalX=0 NormalY=0 NormalZ=1 AngleXU=0 Radius=1.6
  constraints (5):
    c: Equal(g1,g0)
    c: Radius(g1) = 1.6
    c: Symmetric(g1,g0,g-2)
    c: Distance(g1,g-3) = 8
    c: Distance(g0,g1) = 14
FEATURE [PartDesign::Pocket] Pocket015
  BaseFeature = -> Pocket014
  Length = 5
  Length2 = 100
  Midplane = true
  Placement = pos=(0,0,0) rot=(0.57735,0.57735,0.57735;4.18879rad)
  Profile = -> Sketch015
  Type = 1
FEATURE [PartDesign::Pocket] Pocket016
  BaseFeature = -> Pocket015
  Length = 5
  Length2 = 100
  Placement = pos=(0,0,0) rot=(0.57735,0.57735,0.57735;4.18879rad)
  Profile = -> Sketch013
  Type = 1
FEATURE [PartDesign::SubShapeBinder] Binder
  BindMode = 0
  ClaimChildren = false
  Context = -> Part [Body003.Binder.]
  Fuse = false
  MakeFace = true
  PartialLoad = false
  Relative = true
  Support = -> [Body002[Pocket009.Face4]]
  _Version = 2
FEATURE [PartDesign::Plane] DatumPlane021
  Length = 60
  MapMode = 5
  ResizeMode = 0
  Support = -> [XY_Plane009]
  Width = 60
FEATURE [Sketcher::SketchObject] Sketch020
  FullyConstrained = true
  MapMode = 5
  Support = -> [DatumPlane021]
  sketch-geometry (1):
    g0: Circle CenterX=0 CenterY=0 CenterZ=0 NormalX=0 NormalY=0 NormalZ=1 AngleXU=0 Radius=1.45
  constraints (2):
    c: Radius(g0) = 1.45
    c: Coincident(g0,g-1)
FEATURE [PartDesign::Pad] Pad002
  Direction = (1,1,1)
  Length = 1.6
  Length2 = 100
  Profile = -> Sketch020
  Type = 0
FEATURE [PartDesign::Plane] DatumPlane022
  Length = 60
  MapMode = 45
  Placement = pos=(0,-1e-16,1.6) rot=(0,0,1;0rad)
  ResizeMode = 0
  Support = -> [Pad002]
  Width = 60
FEATURE [Sketcher::SketchObject] Sketch021
  FullyConstrained = true
  MapMode = 5
  Support = -> [DatumPlane021]
  sketch-geometry (7):
    g0: LineSegment StartX=0.8 StartY=0.46188 StartZ=0 EndX=1.1e-14 EndY=0.92376 EndZ=0
    g1: LineSegment StartX=1.1e-14 StartY=0.92376 StartZ=0 EndX=-0.8 EndY=0.46188 EndZ=0
    g2: LineSegment StartX=-0.8 StartY=0.46188 StartZ=0 EndX=-0.8 EndY=-0.46188 EndZ=0
    g3: LineSegment StartX=-0.8 StartY=-0.46188 StartZ=0 EndX=4e-15 EndY=-0.92376 EndZ=0
    g4: LineSegment StartX=4e-15 StartY=-0.92376 StartZ=0 EndX=0.8 EndY=-0.46188 EndZ=0
    g5: LineSegment StartX=0.8 StartY=-0.46188 StartZ=0 EndX=0.8 EndY=0.46188 EndZ=0
    g6: Circle CenterX=0 CenterY=0 CenterZ=0 NormalX=0 NormalY=0 NormalZ=1 AngleXU=0 Radius=0.92376
  constraints (16):
    c: Coincident(g0,g1)
    c: Coincident(g1,g2)
    c: Coincident(g2,g3)
    c: Coincident(g3,g4)
    c: Coincident(g4,g5)
    c: Coincident(g5,g0)
    c: Equal(g0, g1-g5) x5
    c: PointOnObject(g0,g6)
    c: PointOnObject(g1,g6)
    c: PointOnObject(g2,g6)
    c: PointOnObject(g3,g6)
    c: PointOnObject(g4,g6)
    c: PointOnObject(g5,g6)
    c: Coincident(g6,g-1)
    c: Distance(g2,g0) = 1.6
    c: Perpendicular(g-1,g2)
FEATURE [PartDesign::Pocket] Pocket022
  BaseFeature = -> Pad002
  Length = 1
  Length2 = 100
  Profile = -> Sketch021
  Reversed = true
  Type = 0
FEATURE [Part::Part2DObjectPython] VThreadProfile  # Draft 2D object (typed FeaturePython)
  Area = 1.40356
  Closed = true
  Continuity = C3
  Instructions = Expand this with the ... button to view instructions | Sweep this object along a helix of the same pitch to produce your thread. | It is recommended to make the helix in the ThreadProfile workbench. | If there is an active Body the ThreadProfile object will be put into it.,If not it can be dragged and dropped into the body later. | If there is an active Body when the helix is made there will be made a ShapeBinder for it | For internal threads you will need to cut the Sweep object out of a cylinder, or if using Part Design sweep it as a Subtractive Pipe. | Always use Frenet mode | I have provided some presets, but it is possible there could be some errors.  Double check for mission critical applications. | Also, the tolerances might be different from what you wish to have.  I believe the internal minor diameters are all minimum and the external are all maximum.
  InternalOrExternal = 1
  MakeFace = true
  MapMode = 5
  MinorDiameter = 1.171
  Parameterization = 1
  Pitch = 0.35
  Placement = pos=(0,-1e-16,1.6) rot=(0,0,1;0rad)
  Points = (719) [(0.584654,0.00510929,0),(0.583797,0.0102044,0),(0.582927,0.0152857,0),(0.582042,0.0203536,0),(0.581139,0.0254084,0),(0.580216,0.0304502,0),+713 more]
  Presets = 6
  Quality = 1
  Support = -> [DatumPlane022]
  ThreadCount = 39.7143
  Version = 1.69
  external_data = [-0.00235387,-0.00461052,-0.00677828,-0.00886428,-0.0108747,-0.0128149,-0.0146895,-0.0165028,-0.0182584,-0.0199597,-0.0216095,-0.0232106,-0.0247653,-0.0262759,-0.0277444,-0.0291725,-0.0305621,-0.0319145,-0.0332313,-0.0345138,-0.0357632,+698 more]
  internal_data = [0,0,0,0,0,0,0,0,0,0,0,0,0,0,0,0,0,0,0,0,0,0,0,0,0,0,0,0,0,0,0,0,0,0,0,0,0,0,0,0,0,0,0,0,0,0,0,0,0,0,0,0,0,0,0,0,0,0,0,0,0,0,0,0,0,0,0,0,0,0,0,0,0,0,0,0,0,0,0,0,0,0,0,0,0,0,0,0,0,0,0,0,0,0,0,0,0,0,0,0,0,0,0,0,0,0,0,0,0,0,0,0,0,0,0,0,0,0,0,0,+599 more]
  preset_names = <blob: 3959 chars omitted>
  presets_data = [0,0,0,2.20878,24.1173,24.6888,0.25,0.693,0.729,0.25,0.793,0.829,0.25,0.893,0.929,0.3,1.032,1.075,0.35,1.171,1.221,0.35,1.371,1.421,0.4,1.509,1.567,0.45,1.648,1.713,0.45,1.948,2.013,0.5,2.387,2.459,0.6,2.764,2.85,0.7,3.141,3.242,0.75,3.58,+712 more]
  expr: ThreadCount = (15.5 - 1.6) / 0.35
FEATURE [Part::Helix] Helix
  Angle = 0
  AttacherType = Attacher::AttachEngine3D
  Height = 13.9
  LocalCoord = 0
  Pitch = 0.35
  Placement = pos=(0,-1e-16,1.6) rot=(0,0,1;0rad)
  Radius = 1
  Style = 0
  expr: Pitch = VThreadProfile.Pitch
  expr: Height = VThreadProfile.ThreadCount * VThreadProfile.Pitch
  expr: .Placement.Base.x = VThreadProfile.Placement.Base.x
  expr: .Placement.Base.y = VThreadProfile.Placement.Base.y
  expr: .Placement.Base.z = VThreadProfile.Placement.Base.z
  expr: .Placement.Rotation.Angle = VThreadProfile.Placement.Rotation.Angle
  expr: .Placement.Rotation.Axis.x = VThreadProfile.Placement.Rotation.Axis.x
  expr: .Placement.Rotation.Axis.y = VThreadProfile.Placement.Rotation.Axis.y
  expr: .Placement.Rotation.Axis.z = VThreadProfile.Placement.Rotation.Axis.z
FEATURE [Part::Helix] Helix001
  Angle = 0
  AttacherType = Attacher::AttachEngine3D
  Height = 13.9
  LocalCoord = 0
  Pitch = 0.35
  Placement = pos=(0,-1e-16,1.6) rot=(0,0,1;0rad)
  Radius = 1
  Style = 0
  expr: Pitch = VThreadProfile.Pitch
  expr: Height = VThreadProfile.ThreadCount * VThreadProfile.Pitch
  expr: .Placement.Base.x = VThreadProfile.Placement.Base.x
  expr: .Placement.Base.y = VThreadProfile.Placement.Base.y
  expr: .Placement.Base.z = VThreadProfile.Placement.Base.z
  expr: .Placement.Rotation.Angle = VThreadProfile.Placement.Rotation.Angle
  expr: .Placement.Rotation.Axis.x = VThreadProfile.Placement.Rotation.Axis.x
  expr: .Placement.Rotation.Axis.y = VThreadProfile.Placement.Rotation.Axis.y
  expr: .Placement.Rotation.Axis.z = VThreadProfile.Placement.Rotation.Axis.z
FEATURE [PartDesign::ShapeBinder] ShapeBinder001
  Placement = pos=(0,-1e-16,1.6) rot=(0,0,1;0rad)
  Support = -> [Helix001]
  TraceSupport = false
FEATURE [PartDesign::AdditivePipe] AdditivePipe
  AuxilleryCurvelinear = true
  AuxillerySpineTangent = false
  BaseFeature = -> Pocket022
  Binormal = (0,0,0)
  Mode = 2
  Profile = -> VThreadProfile
  Spine = -> ShapeBinder001 [Edge1,Edge2,Edge3,Edge4,Edge5,Edge6,Edge7,Edge8,Edge9,Edge10,Edge11,Edge12,Edge13,Edge14,Edge15,Edge16,Edge17,Edge18,Edge19,Edge20,Edge21,Edge22,Edge23,Edge24,Edge25,Edge26,Edge27,Edge28,Edge29,Edge30,Edge31,Edge32,Edge33,Edge34,Edge35,Edge36,Edge37,Edge38,Edge39,Edge40]
  SpineTangent = false
  Transformation = 0
  Transition = 0
FEATURE [PartDesign::Body] Body008  label="screw1"
  Group = -> [DatumPlane021,Sketch020,Pad002,DatumPlane022,Sketch021,Pocket022,VThreadProfile,ShapeBinder001,AdditivePipe]
  Origin = -> Origin009
  Placement = pos=(-8,0,12.9) rot=(0,0,-1;5.75959rad)
  Tip = -> AdditivePipe
FEATURE [PartDesign::FeatureBase] Clone003
  BaseFeature = -> Body008
FEATURE [PartDesign::Body] Body009  label="screw2"
  BaseFeature = -> Body008
  Group = -> [Clone003]
  Origin = -> Origin010
  Placement = pos=(8,0,12.9) rot=(0,0,-1;6.02139rad)
  Tip = -> Clone003
FEATURE [Part::Part2DObjectPython] VThreadProfile001  # Draft 2D object (typed FeaturePython)
  Area = 21.5648
  Closed = true
  Continuity = C3
  Instructions = <same value as first occurrence — deduplicated (x15 in doc)>
  InternalOrExternal = 1
  MakeFace = true
  MapMode = 11
  MinorDiameter = 4.773
  Parameterization = 1
  Pitch = 1
  Placement = pos=(0,-2e-15,9) rot=(0,0,1;1.5708rad)
  Points = (719) [(2.38406,0.0208343,0),(2.38153,0.0416275,0),(2.3789,0.0623805,0),(2.37618,0.0830937,0),(2.37336,0.103767,0),(2.37042,0.124402,0),(2.36737,0.144997,0),+712 more]
  Presets = 16
  Quality = 1
  ThreadCount = 4
  Version = 1.69
  external_data = <same value as first occurrence — deduplicated (x15 in doc)>
  internal_data = <same value as first occurrence — deduplicated (x15 in doc)>
  preset_names = <blob: 3959 chars omitted>
  presets_data = <same value as first occurrence — deduplicated (x15 in doc)>
FEATURE [Part::Helix] Helix002
  Angle = 0
  AttacherType = Attacher::AttachEngine3D
  Height = 4
  LocalCoord = 0
  Pitch = 1
  Placement = pos=(0,-2e-15,9) rot=(0,0,1;1.5708rad)
  Radius = 1
  Style = 0
  expr: Pitch = VThreadProfile001.Pitch
  expr: Height = VThreadProfile001.ThreadCount * VThreadProfile001.Pitch
  expr: .Placement.Base.x = VThreadProfile001.Placement.Base.x
  expr: .Placement.Base.y = VThreadProfile001.Placement.Base.y
  expr: .Placement.Base.z = VThreadProfile001.Placement.Base.z
  expr: .Placement.Rotation.Angle = VThreadProfile001.Placement.Rotation.Angle
  expr: .Placement.Rotation.Axis.x = VThreadProfile001.Placement.Rotation.Axis.x
  expr: .Placement.Rotation.Axis.y = VThreadProfile001.Placement.Rotation.Axis.y
  expr: .Placement.Rotation.Axis.z = VThreadProfile001.Placement.Rotation.Axis.z
FEATURE [PartDesign::ShapeBinder] ShapeBinder002
  Placement = pos=(0,-2e-15,9) rot=(0,0,1;1.5708rad)
  Support = -> [Helix002]
  TraceSupport = false
FEATURE [PartDesign::AdditivePipe] AdditivePipe001
  AuxilleryCurvelinear = true
  AuxillerySpineTangent = false
  BaseFeature = -> Pocket
  Binormal = (0,0,0)
  Mode = 2
  Placement = pos=(0,0,0) rot=(0.57735,0.57735,0.57735;4.18879rad)
  Profile = -> VThreadProfile001
  Spine = -> ShapeBinder002 [Edge1,Edge2,Edge3,Edge4]
  SpineTangent = false
  Transformation = 0
  Transition = 0
FEATURE [PartDesign::Plane] DatumPlane034
  Length = 62.6886
  MapMode = 5
  Placement = pos=(0,0,0) rot=(0.57735,0.57735,0.57735;2.0944rad)
  ResizeMode = 0
  Support = -> [YZ_Plane012]
  Width = 93.1886
FEATURE [Sketcher::SketchObject] Sketch025
  FullyConstrained = true
  MapMode = 5
  Placement = pos=(0,0,0) rot=(0.57735,0.57735,0.57735;2.0944rad)
  Support = -> [DatumPlane034]
  sketch-geometry (18):
    g0: LineSegment StartX=-2.1 StartY=49.4 StartZ=0 EndX=-2.1 EndY=60.7 EndZ=0
    g1: LineSegment StartX=-7.95 StartY=68.2 StartZ=0 EndX=-7.95 EndY=64.5 EndZ=0
    g2: LineSegment StartX=-7.95 StartY=64.5 StartZ=0 EndX=-6 EndY=64.5 EndZ=0
    g3: LineSegment StartX=-6 StartY=64.5 StartZ=0 EndX=-6 EndY=58.5 EndZ=0
    g4: LineSegment StartX=-6 StartY=58.5 StartZ=0 EndX=-7.95 EndY=58.5 EndZ=0
    g5: LineSegment StartX=-7.95 StartY=58.5 StartZ=0 EndX=-7.95 EndY=55.5 EndZ=0
    g6: LineSegment StartX=-7.95 StartY=55.5 StartZ=0 EndX=-2.2 EndY=55.5 EndZ=0
    g7: LineSegment StartX=-2.2 StartY=55.5 StartZ=0 EndX=-2.2 EndY=49.4 EndZ=0
    g8: LineSegment StartX=-2.2 StartY=49.4 StartZ=0 EndX=-2.1 EndY=49.4 EndZ=0
    g9: LineSegment StartX=-3.2 StartY=68.2 StartZ=0 EndX=-3.2 EndY=61.2 EndZ=0
    g10: LineSegment StartX=-3.9 StartY=68.2 StartZ=0 EndX=-3.9 EndY=61.2 EndZ=0
    g11: LineSegment StartX=-3.9 StartY=61.2 StartZ=0 EndX=-2.6 EndY=61.2 EndZ=0
    g12: LineSegment StartX=-3.9 StartY=68.2 StartZ=0 EndX=-7.95 EndY=68.2 EndZ=0
    g13: LineSegment StartX=-3.9 StartY=68.2 StartZ=0 EndX=-3.7 EndY=68.2 EndZ=0
    g14: LineSegment StartX=-3.7 StartY=68.2 StartZ=0 EndX=-3.2 EndY=67.7 EndZ=0
    g15: LineSegment StartX=-3.2 StartY=67.7 StartZ=0 EndX=-3.2 EndY=66.2 EndZ=0
    g16: LineSegment StartX=-3.2 StartY=66.2 StartZ=0 EndX=-3.9 EndY=61.2 EndZ=0
    g17: LineSegment StartX=-2.6 StartY=61.2 StartZ=0 EndX=-2.1 EndY=60.7 EndZ=0
  constraints (54):
    c: Vertical(g0)
    c: Coincident(g12,g1)
    c: Vertical(g1)
    c: Coincident(g1,g2)
    c: Horizontal(g2)
    c: Coincident(g2,g3)
    c: Vertical(g3)
    c: Coincident(g3,g4)
    c: Horizontal(g4)
    c: Coincident(g4,g5)
    c: Vertical(g5)
    c: Coincident(g5,g6)
    c: Horizontal(g6)
    c: Coincident(g6,g7)
    c: Vertical(g7)
    c: Coincident(g7,g8)
    c: Coincident(g8,g0)
    c: Horizontal(g8)
    c: Distance(g0,g-2) = 2.1
    c: Distance(g7,g-2) = 2.2
    c: Distance(g12,g-2) = 7.95
    c: Distance(g1) = 3.7
    c: Vertical(g4,g1)
    c: Distance(g2,g-2) = 6
    c: Distance(g3) = 6
    c: Vertical(g9)
    c: Distance(g9) = 7
    c: Distance(g9,g-2) = 3.2
    c: Vertical(g10)
    c: Distance(g10,g-2) = 3.9
    c: Coincident(g11,g10)
    c: Horizontal(g11)
    c: Equal(g10,g9)
    c: Coincident(g12,g10)
    c: Horizontal(g12)
    c: PointOnObject(g9,g11)
    c: Coincident(g12,g13)
    c: Horizontal(g13)
    c: Coincident(g13,g14)
    c: PointOnObject(g14,g9)
    c: Coincident(g14,g15)
    c: PointOnObject(g15,g9)
    c: Coincident(g15,g16)
    c: Coincident(g16,g11)
    c: Distance(g15,g12) = 2
    c: Angle(g12,g14) = 2.35619
    c: Distance(g14,g12) = 0.5
    c: Distance(g0,g12) = 18.8
    c: Angle(g11,g17) = 2.35619
    c: Distance(g17,g11) = 0.5
    c: Coincident(g11,g17)
    c: Coincident(g0,g17)
    c: Distance(g5) = 3
    c: Distance(g5,g-1) = 55.5
FEATURE [PartDesign::Plane] DatumPlane035
  Length = 60
  MapMode = 5
  Placement = pos=(-2.46e-14,9.2e-15,55.5) rot=(0,0,1;0rad)
  ResizeMode = 0
  Support = -> [Revolution002]
  Width = 60
FEATURE [PartDesign::Revolution] Revolution003
  Angle = 360
  Axis = (-1e-16,1e-16,1)
  Base = (0,0,0)
  Placement = pos=(0,0,0) rot=(0.57735,0.57735,0.57735;2.0944rad)
  Profile = -> Sketch025
  ReferenceAxis = -> Sketch025 [V_Axis]
FEATURE [PartDesign::Plane] DatumPlane036
  AttachmentOffset = pos=(0,0,0) rot=(1,0,0;1.5708rad)
  Length = 63.6528
  MapMode = 7
  Placement = pos=(-6.7e-15,-7.95,68.2) rot=(1,0,0;1.5708rad)
  ResizeMode = 0
  Support = -> [Revolution003]
  Width = 106.853
FEATURE [Sketcher::SketchObject] Sketch026
  ExternalGeometry = -> [Revolution003]
  FullyConstrained = true
  MapMode = 5
  Placement = pos=(-6.7e-15,-7.95,68.2) rot=(1,0,0;1.5708rad)
  Support = -> [DatumPlane036]
  sketch-geometry (8):
    g0: LineSegment StartX=-7 StartY=-11.5 StartZ=0 EndX=-9 EndY=-11.5 EndZ=0
    g1: LineSegment StartX=-9 StartY=-11.5 StartZ=0 EndX=-9 EndY=-9.7 EndZ=0
    g2: LineSegment StartX=-9 StartY=-9.7 StartZ=0 EndX=-7 EndY=-9.7 EndZ=0
    g3: LineSegment StartX=-7 StartY=-9.7 StartZ=0 EndX=-7 EndY=-11.5 EndZ=0
    g4: LineSegment StartX=7 StartY=-11.5 StartZ=0 EndX=9 EndY=-11.5 EndZ=0
    g5: LineSegment StartX=9 StartY=-11.5 StartZ=0 EndX=9 EndY=-9.7 EndZ=0
    g6: LineSegment StartX=9 StartY=-9.7 StartZ=0 EndX=7 EndY=-9.7 EndZ=0
    g7: LineSegment StartX=7 StartY=-9.7 StartZ=0 EndX=7 EndY=-11.5 EndZ=0
  constraints (23):
    c: Coincident(g0,g1)
    c: Coincident(g1,g2)
    c: Coincident(g2,g3)
    c: Coincident(g3,g0)
    c: Horizontal(g0)
    c: Horizontal(g2)
    c: Vertical(g1)
    c: Coincident(g4,g5)
    c: Coincident(g5,g6)
    c: Coincident(g6,g7)
    c: Coincident(g7,g4)
    c: Horizontal(g4)
    c: Horizontal(g6)
    c: Vertical(g5)
    c: Equal(g6,g2)
    c: Equal(g5,g1)
    c: Distance(g7) = 1.8
    c: Vertical(g3)
    c: Vertical(g7)
    c: Distance(g2,g6) = 14
    c: Symmetric(g2,g6,g-2)
    c: Distance(g6,g-1) = 9.7
    c: Distance(g6) = 2
FEATURE [PartDesign::Pocket] Pocket029
  BaseFeature = -> Revolution003
  Length = 5
  Length2 = 100
  Placement = pos=(0,0,0) rot=(0.57735,0.57735,0.57735;2.0944rad)
  Profile = -> Sketch026
  Type = 1
FEATURE [Part::Helix] Helix014
  Angle = 0
  AttacherType = Attacher::AttachEngine3D
  Height = 6.125
  LocalCoord = 0
  Pitch = 1.25
  Placement = pos=(-5.9e-15,-6.2e-15,55.5) rot=(0,1,0;3.14159rad)
  Radius = 1
  Style = 0
  expr: .Placement.Rotation.Axis.z = VThreadProfile012.Placement.Rotation.Axis.z
  expr: .Placement.Rotation.Axis.y = VThreadProfile012.Placement.Rotation.Axis.y
  expr: .Placement.Rotation.Axis.x = VThreadProfile012.Placement.Rotation.Axis.x
  expr: .Placement.Rotation.Angle = VThreadProfile012.Placement.Rotation.Angle
  expr: .Placement.Base.z = VThreadProfile012.Placement.Base.z
  expr: .Placement.Base.y = VThreadProfile012.Placement.Base.y
  expr: .Placement.Base.x = VThreadProfile012.Placement.Base.x
  expr: Height = VThreadProfile012.ThreadCount * VThreadProfile012.Pitch
  expr: Pitch = VThreadProfile012.Pitch
FEATURE [Part::Helix] Helix015
  Angle = 0
  AttacherType = Attacher::AttachEngine3D
  Height = 6.125
  LocalCoord = 0
  Pitch = 1.25
  Placement = pos=(-5.9e-15,-6.2e-15,55.5) rot=(0,1,0;3.14159rad)
  Radius = 1
  Style = 0
  expr: .Placement.Rotation.Axis.z = VThreadProfile012.Placement.Rotation.Axis.z
  expr: .Placement.Rotation.Axis.y = VThreadProfile012.Placement.Rotation.Axis.y
  expr: .Placement.Rotation.Axis.x = VThreadProfile012.Placement.Rotation.Axis.x
  expr: .Placement.Rotation.Angle = VThreadProfile012.Placement.Rotation.Angle
  expr: .Placement.Base.z = VThreadProfile012.Placement.Base.z
  expr: .Placement.Base.y = VThreadProfile012.Placement.Base.y
  expr: .Placement.Base.x = VThreadProfile012.Placement.Base.x
  expr: Height = VThreadProfile012.ThreadCount * VThreadProfile012.Pitch
  expr: Pitch = VThreadProfile012.Pitch
FEATURE [Part::Helix] Helix016
  Angle = 0
  AttacherType = Attacher::AttachEngine3D
  Height = 6.125
  LocalCoord = 0
  Pitch = 1.25
  Placement = pos=(-5.9e-15,-6.2e-15,55.5) rot=(0,1,0;3.14159rad)
  Radius = 1
  Style = 0
  expr: .Placement.Rotation.Axis.z = VThreadProfile012.Placement.Rotation.Axis.z
  expr: .Placement.Rotation.Axis.y = VThreadProfile012.Placement.Rotation.Axis.y
  expr: .Placement.Rotation.Axis.x = VThreadProfile012.Placement.Rotation.Axis.x
  expr: .Placement.Rotation.Angle = VThreadProfile012.Placement.Rotation.Angle
  expr: .Placement.Base.z = VThreadProfile012.Placement.Base.z
  expr: .Placement.Base.y = VThreadProfile012.Placement.Base.y
  expr: .Placement.Base.x = VThreadProfile012.Placement.Base.x
  expr: Height = VThreadProfile012.ThreadCount * VThreadProfile012.Pitch
  expr: Pitch = VThreadProfile012.Pitch
FEATURE [PartDesign::Plane] DatumPlane037
  AttachmentOffset = pos=(0,0,0) rot=(0,1,0;3.14159rad)
  Length = 60
  MapMode = 11
  Placement = pos=(-5.9e-15,-6.2e-15,55.5) rot=(0,1,0;3.14159rad)
  ResizeMode = 0
  Support = -> [Pocket029]
  Width = 60
FEATURE [Part::Part2DObjectPython] VThreadProfile012  # Draft 2D object (typed FeaturePython)
  Area = 39.0125
  Closed = true
  Continuity = C3
  Instructions = <same value as first occurrence — deduplicated (x15 in doc)>
  InternalOrExternal = 1
  MakeFace = true
  MapMode = 5
  MinorDiameter = 6.466
  Parameterization = 1
  Pitch = 1.25
  Placement = pos=(-5.9e-15,-6.2e-15,55.5) rot=(0,1,0;3.14159rad)
  Points = (719) [(3.22993,0.0282264,0),(3.22674,0.0564014,0),(3.22342,0.0845257,0),(3.21995,0.1126,0),(3.21633,0.140624,0),(3.21256,0.168598,0),(3.20863,0.196522,0),+712 more]
  Presets = 18
  Quality = 1
  Support = -> [DatumPlane037]
  ThreadCount = 4.9
  Version = 1.69
  external_data = <same value as first occurrence — deduplicated (x15 in doc)>
  internal_data = <same value as first occurrence — deduplicated (x15 in doc)>
  preset_names = <blob: 3959 chars omitted>
  presets_data = <same value as first occurrence — deduplicated (x15 in doc)>
FEATURE [Part::Helix] Helix017
  Angle = 0
  AttacherType = Attacher::AttachEngine3D
  Height = 6.125
  LocalCoord = 0
  Pitch = 1.25
  Placement = pos=(-5.9e-15,-6.2e-15,55.5) rot=(0,1,0;3.14159rad)
  Radius = 1
  Style = 0
  expr: .Placement.Rotation.Axis.z = VThreadProfile012.Placement.Rotation.Axis.z
  expr: .Placement.Rotation.Axis.y = VThreadProfile012.Placement.Rotation.Axis.y
  expr: .Placement.Rotation.Axis.x = VThreadProfile012.Placement.Rotation.Axis.x
  expr: .Placement.Rotation.Angle = VThreadProfile012.Placement.Rotation.Angle
  expr: .Placement.Base.z = VThreadProfile012.Placement.Base.z
  expr: .Placement.Base.y = VThreadProfile012.Placement.Base.y
  expr: .Placement.Base.x = VThreadProfile012.Placement.Base.x
  expr: Height = VThreadProfile012.ThreadCount * VThreadProfile012.Pitch
  expr: Pitch = VThreadProfile012.Pitch
FEATURE [PartDesign::ShapeBinder] ShapeBinder013
  Placement = pos=(-5.9e-15,-6.2e-15,55.5) rot=(0,1,0;3.14159rad)
  Support = -> [Helix017]
  TraceSupport = false
FEATURE [PartDesign::AdditivePipe] AdditivePipe003
  AuxilleryCurvelinear = true
  AuxillerySpineTangent = false
  BaseFeature = -> Pocket029
  Binormal = (0,0,0)
  Mode = 2
  Placement = pos=(0,0,0) rot=(0.57735,0.57735,0.57735;2.0944rad)
  Profile = -> VThreadProfile012
  Spine = -> ShapeBinder013 [Edge1,Edge2,Edge3,Edge4,Edge5]
  SpineTangent = false
  Transformation = 0
  Transition = 0
FEATURE [PartDesign::Pocket] Pocket030
  BaseFeature = -> AdditivePipe003
  Length = 5
  Length2 = 100
  Placement = pos=(0,0,0) rot=(0.57735,0.57735,0.57735;2.0944rad)
  Profile = -> AdditivePipe003 [Face20]
  Type = 1
FEATURE [PartDesign::Body] Body011  label="e3dmount"
  Group = -> [DatumPlane034,Sketch025,DatumPlane035,Revolution003,DatumPlane036,Sketch026,Pocket029,VThreadProfile012,DatumPlane037,ShapeBinder013,AdditivePipe003,Pocket030]
  Origin = -> Origin012
  Placement = pos=(0,0,0) rot=(0,0,-1;1.5708rad)
  Tip = -> Pocket030
FEATURE [PartDesign::Plane] DatumPlane017
  Length = 60
  MapMode = 5
  Placement = pos=(-2.46e-14,-8.32e-14,55.5) rot=(0,0,1;0rad)
  ResizeMode = 0
  Support = -> [Pocket016]
  Width = 60
FEATURE [Sketcher::SketchObject] Sketch017
  FullyConstrained = true
  MapMode = 5
  Placement = pos=(-2.46e-14,-8.32e-14,55.5) rot=(0,0,1;0rad)
  Support = -> [DatumPlane017]
  sketch-geometry (4):
    g0: Circle CenterX=-7 CenterY=3.75 CenterZ=0 NormalX=0 NormalY=0 NormalZ=1 AngleXU=0 Radius=1.18
    g1: Circle CenterX=-7 CenterY=-3.75 CenterZ=0 NormalX=0 NormalY=0 NormalZ=1 AngleXU=0 Radius=1.18
    g2: Circle CenterX=7 CenterY=3.75 CenterZ=0 NormalX=0 NormalY=0 NormalZ=1 AngleXU=0 Radius=1.18
    g3: Circle CenterX=7 CenterY=-3.75 CenterZ=0 NormalX=0 NormalY=0 NormalZ=1 AngleXU=0 Radius=1.18
  constraints (10):
    c: Symmetric(g0,g2,g-2)
    c: Symmetric(g0,g1,g-1)
    c: Vertical(g2,g3)
    c: Horizontal(g3,g1)
    c: Equal(g0,g2)
    c: Equal(g2,g3)
    c: Equal(g3,g1)
    c: Radius(g2) = 1.18
    c: Distance(g0,g2) = 14
    c: Distance(g2,g3) = 7.5
FEATURE [PartDesign::Pocket] Pocket019
  BaseFeature = -> Pocket016
  Length = 6
  Length2 = 100
  Placement = pos=(0,0,0) rot=(0.57735,0.57735,0.57735;4.18879rad)
  Profile = -> Sketch017
  Type = 0
FEATURE [PartDesign::Plane] DatumPlane041
  Length = 60
  MapMode = 5
  Placement = pos=(-1.04e-14,-4.17e-14,23.5) rot=(0,1,0;3.14159rad)
  ResizeMode = 0
  Support = -> [Pocket019]
  Width = 60
FEATURE [Sketcher::SketchObject] Sketch016
  ExternalGeometry = -> [Binder]
  FullyConstrained = false
  MapMode = 5
  Placement = pos=(-1.04e-14,-4.17e-14,23.5) rot=(0,1,0;3.14159rad)
  Support = -> [DatumPlane041]
  sketch-geometry (4):
    g0: Circle CenterX=-6 CenterY=3 CenterZ=0 NormalX=0 NormalY=0 NormalZ=1 AngleXU=0 Radius=1
    g1: Circle CenterX=6 CenterY=3 CenterZ=0 NormalX=0 NormalY=0 NormalZ=1 AngleXU=0 Radius=1
    g2: Circle CenterX=6 CenterY=-3 CenterZ=0 NormalX=0 NormalY=0 NormalZ=1 AngleXU=0 Radius=1
    g3: Circle CenterX=-6 CenterY=-3 CenterZ=0 NormalX=0 NormalY=0 NormalZ=1 AngleXU=0 Radius=1
  constraints (3):
    c: Equal(g3,g0)
    c: Equal(g0,g1)
    c: Equal(g1,g2)
FEATURE [PartDesign::Pocket] Pocket032
  BaseFeature = -> Pocket019
  Length = 2.5
  Length2 = 100
  Placement = pos=(0,0,0) rot=(0.57735,0.57735,0.57735;4.18879rad)
  Profile = -> Sketch016
  Type = 0
FEATURE [Sketcher::SketchObject] Sketch027
  ExternalGeometry = -> [Binder]
  FullyConstrained = false
  MapMode = 5
  Placement = pos=(-1.04e-14,-4.17e-14,23.5) rot=(0,1,0;3.14159rad)
  Support = -> [DatumPlane041]
  sketch-geometry (2):
    g0: Circle CenterX=-8 CenterY=0 CenterZ=0 NormalX=0 NormalY=0 NormalZ=1 AngleXU=0 Radius=0.5
    g1: Circle CenterX=8 CenterY=0 CenterZ=0 NormalX=0 NormalY=0 NormalZ=1 AngleXU=0 Radius=0.5
  constraints (2):
    c: Equal(g1,g0)
    c: Radius(g1) = 0.5
FEATURE [PartDesign::Pocket] Pocket033
  BaseFeature = -> Pocket032
  Length = 4
  Length2 = 100
  Placement = pos=(0,0,0) rot=(0.57735,0.57735,0.57735;4.18879rad)
  Profile = -> Sketch027
  Type = 0
FEATURE [PartDesign::Plane] DatumPlane042
  AttachmentOffset = pos=(0,0,0) rot=(0,1,0;3.14159rad)
  Length = 60
  MapMode = 11
  Placement = pos=(-8,-4.5e-14,23.5) rot=(0,0,1;4.71239rad)
  ResizeMode = 0
  Support = -> [Pocket033]
  Width = 60
FEATURE [Part::Part2DObjectPython] VThreadProfile016  # Draft 2D object (typed FeaturePython)
  Area = 1.53249
  Closed = true
  Continuity = C3
  Instructions = <same value as first occurrence — deduplicated (x15 in doc)>
  InternalOrExternal = 0
  MakeFace = true
  MapMode = 2
  MinorDiameter = 1.221
  Parameterization = 1
  Pitch = 0.35
  Placement = pos=(-8,-4.5e-14,23.5) rot=(0,0,-1;1.5708rad)
  Points = (719) [(0.610477,0.00533496,0),(0.610407,0.0106695,0),(0.61029,0.0160032,0),(0.610127,0.0213358,0),(0.609917,0.0266666,0),(0.609661,0.0319955,0),+713 more]
  Presets = 6
  Quality = 1
  Support = -> [DatumPlane042]
  ThreadCount = 14.2
  Version = 1.69
  external_data = <same value as first occurrence — deduplicated (x15 in doc)>
  internal_data = <same value as first occurrence — deduplicated (x15 in doc)>
  preset_names = <blob: 3959 chars omitted>
  presets_data = <same value as first occurrence — deduplicated (x15 in doc)>
FEATURE [Part::Helix] Helix021
  Angle = 0
  AttacherType = Attacher::AttachEngine3D
  Height = 4.97
  LocalCoord = 0
  Pitch = 0.35
  Placement = pos=(-8,-4.5e-14,23.5) rot=(0,0,-1;1.5708rad)
  Radius = 1
  Style = 0
  expr: Pitch = VThreadProfile016.Pitch
  expr: Height = VThreadProfile016.ThreadCount * VThreadProfile016.Pitch
  expr: .Placement.Base.x = VThreadProfile016.Placement.Base.x
  expr: .Placement.Base.y = VThreadProfile016.Placement.Base.y
  expr: .Placement.Base.z = VThreadProfile016.Placement.Base.z
  expr: .Placement.Rotation.Angle = VThreadProfile016.Placement.Rotation.Angle
  expr: .Placement.Rotation.Axis.x = VThreadProfile016.Placement.Rotation.Axis.x
  expr: .Placement.Rotation.Axis.y = VThreadProfile016.Placement.Rotation.Axis.y
  expr: .Placement.Rotation.Axis.z = VThreadProfile016.Placement.Rotation.Axis.z
FEATURE [PartDesign::ShapeBinder] ShapeBinder017
  Placement = pos=(-8,-4.5e-14,23.5) rot=(0,0,-1;1.5708rad)
  Support = -> [Helix021]
  TraceSupport = false
FEATURE [PartDesign::SubtractivePipe] SubtractivePipe012
  AuxilleryCurvelinear = true
  AuxillerySpineTangent = false
  BaseFeature = -> Pocket033
  Binormal = (0,0,0)
  Mode = 2
  Placement = pos=(0,0,0) rot=(0.57735,0.57735,0.57735;4.18879rad)
  Profile = -> VThreadProfile016
  Spine = -> ShapeBinder017 [Edge1,Edge2,Edge3,Edge4,Edge5,Edge6,Edge7,Edge8,Edge9,Edge10,Edge11,Edge12,Edge13,Edge14,Edge15]
  SpineTangent = false
  Transformation = 0
  Transition = 0
FEATURE [PartDesign::Plane] DatumPlane043
  AttachmentOffset = pos=(0,0,0) rot=(0,1,0;3.14159rad)
  Length = 60
  MapMode = 11
  Placement = pos=(8,-5.13e-14,23.5) rot=(0,0,1;4.71239rad)
  ResizeMode = 0
  Support = -> [Pocket033]
  Width = 60
FEATURE [Part::Part2DObjectPython] VThreadProfile017  # Draft 2D object (typed FeaturePython)
  Area = 1.53249
  Closed = true
  Continuity = C3
  Instructions = <same value as first occurrence — deduplicated (x15 in doc)>
  InternalOrExternal = 0
  MakeFace = true
  MapMode = 5
  MinorDiameter = 1.221
  Parameterization = 1
  Pitch = 0.35
  Placement = pos=(8,-5.13e-14,23.5) rot=(0,0,-1;1.5708rad)
  Points = (719) [(0.610477,0.00533496,0),(0.610407,0.0106695,0),(0.61029,0.0160032,0),(0.610127,0.0213358,0),(0.609917,0.0266666,0),(0.609661,0.0319955,0),+713 more]
  Presets = 6
  Quality = 1
  Support = -> [DatumPlane043]
  ThreadCount = 14.2
  Version = 1.69
  external_data = <same value as first occurrence — deduplicated (x15 in doc)>
  internal_data = <same value as first occurrence — deduplicated (x15 in doc)>
  preset_names = <blob: 3959 chars omitted>
  presets_data = <same value as first occurrence — deduplicated (x15 in doc)>
FEATURE [Part::Helix] Helix022
  Angle = 0
  AttacherType = Attacher::AttachEngine3D
  Height = 4.97
  LocalCoord = 0
  Pitch = 0.35
  Placement = pos=(8,-5.13e-14,23.5) rot=(0,0,-1;1.5708rad)
  Radius = 1
  Style = 0
  expr: .Placement.Rotation.Axis.z = VThreadProfile017.Placement.Rotation.Axis.z
  expr: .Placement.Rotation.Axis.y = VThreadProfile017.Placement.Rotation.Axis.y
  expr: .Placement.Rotation.Axis.x = VThreadProfile017.Placement.Rotation.Axis.x
  expr: .Placement.Rotation.Angle = VThreadProfile017.Placement.Rotation.Angle
  expr: .Placement.Base.z = VThreadProfile017.Placement.Base.z
  expr: .Placement.Base.y = VThreadProfile017.Placement.Base.y
  expr: .Placement.Base.x = VThreadProfile017.Placement.Base.x
  expr: Height = VThreadProfile017.ThreadCount * VThreadProfile017.Pitch
  expr: Pitch = VThreadProfile017.Pitch
FEATURE [PartDesign::ShapeBinder] ShapeBinder018
  Placement = pos=(8,-5.13e-14,23.5) rot=(0,0,-1;1.5708rad)
  Support = -> [Helix022]
  TraceSupport = false
FEATURE [PartDesign::SubtractivePipe] SubtractivePipe013
  AuxilleryCurvelinear = true
  AuxillerySpineTangent = false
  BaseFeature = -> SubtractivePipe012
  Binormal = (0,0,0)
  Mode = 2
  Placement = pos=(0,0,0) rot=(0.57735,0.57735,0.57735;4.18879rad)
  Profile = -> VThreadProfile017
  Spine = -> ShapeBinder018 [Edge1,Edge2,Edge3,Edge4,Edge5,Edge6,Edge7,Edge8,Edge9,Edge10,Edge11,Edge12,Edge13,Edge14,Edge15]
  SpineTangent = false
  Transformation = 0
  Transition = 0
FEATURE [PartDesign::Plane] DatumPlane044
  Length = 60
  MapMode = 11
  Placement = pos=(1.53e-14,-1.191e-13,55.5) rot=(0.707107,0.707107,0;3.14159rad)
  ResizeMode = 0
  Support = -> [Pocket033]
  Width = 60
FEATURE [Part::Part2DObjectPython] VThreadProfile018  # Draft 2D object (typed FeaturePython)
  Area = 41.4736
  Closed = true
  Continuity = C3
  Instructions = <same value as first occurrence — deduplicated (x15 in doc)>
  InternalOrExternal = 0
  MakeFace = true
  MapMode = 2
  MinorDiameter = 6.647
  Parameterization = 1
  Pitch = 1.25
  Placement = pos=(1.53e-14,-1.191e-13,55.5) rot=(0.707107,0.707107,0;3.14159rad)
  Points = (719) [(3.32337,0.029043,0),(3.32299,0.0580837,0),(3.32236,0.0871201,0),(3.32147,0.11615,0),(3.32033,0.145171,0),(3.31893,0.17418,0),(3.31728,0.203177,0),+712 more]
  Presets = 18
  Quality = 1
  Support = -> [DatumPlane044]
  ThreadCount = 5.44
  Version = 1.69
  external_data = <same value as first occurrence — deduplicated (x15 in doc)>
  internal_data = <same value as first occurrence — deduplicated (x15 in doc)>
  preset_names = <blob: 3959 chars omitted>
  presets_data = <same value as first occurrence — deduplicated (x15 in doc)>
FEATURE [Part::Helix] Helix023
  Angle = 0
  AttacherType = Attacher::AttachEngine3D
  Height = 6.8
  LocalCoord = 0
  Pitch = 1.25
  Placement = pos=(1.53e-14,-1.191e-13,55.5) rot=(0.707107,0.707107,0;3.14159rad)
  Radius = 1
  Style = 0
  expr: .Placement.Rotation.Axis.z = VThreadProfile018.Placement.Rotation.Axis.z
  expr: .Placement.Rotation.Axis.y = VThreadProfile018.Placement.Rotation.Axis.y
  expr: .Placement.Rotation.Axis.x = VThreadProfile018.Placement.Rotation.Axis.x
  expr: .Placement.Rotation.Angle = VThreadProfile018.Placement.Rotation.Angle
  expr: .Placement.Base.z = VThreadProfile018.Placement.Base.z
  expr: .Placement.Base.y = VThreadProfile018.Placement.Base.y
  expr: .Placement.Base.x = VThreadProfile018.Placement.Base.x
  expr: Height = VThreadProfile018.ThreadCount * VThreadProfile018.Pitch
  expr: Pitch = VThreadProfile018.Pitch
FEATURE [PartDesign::ShapeBinder] ShapeBinder019
  Placement = pos=(1.53e-14,-1.191e-13,55.5) rot=(0.707107,0.707107,0;3.14159rad)
  Support = -> [Helix023]
  TraceSupport = false
FEATURE [PartDesign::SubtractivePipe] SubtractivePipe014
  AuxilleryCurvelinear = true
  AuxillerySpineTangent = false
  BaseFeature = -> SubtractivePipe013
  Binormal = (0,0,0)
  Mode = 2
  Placement = pos=(0,0,0) rot=(0.57735,0.57735,0.57735;4.18879rad)
  Profile = -> VThreadProfile018
  Spine = -> ShapeBinder019
  SpineTangent = false
  Transformation = 0
  Transition = 0
FEATURE [PartDesign::Plane] DatumPlane045
  AttachmentOffset = pos=(0,0,0) rot=(0,1,0;3.14159rad)
  Length = 60.0001
  MapMode = 45
  Placement = pos=(-7,3.75,55.5) rot=(1e-06,1,0;3.14159rad)
  ResizeMode = 0
  Support = -> [Pocket033]
  Width = 60.0001
FEATURE [Part::Part2DObjectPython] VThreadProfile019  # Draft 2D object (typed FeaturePython)
  Area = 5.75678
  Closed = true
  Continuity = C3
  Instructions = <same value as first occurrence — deduplicated (x15 in doc)>
  InternalOrExternal = 0
  MakeFace = true
  MapMode = 2
  MinorDiameter = 2.459
  Parameterization = 1
  Pitch = 0.5
  Placement = pos=(-7,3.75,55.5) rot=(1e-06,1,0;3.14159rad)
  Points = (719) [(1.22945,0.0107442,0),(1.22931,0.0214876,0),(1.22908,0.0322293,0),(1.22875,0.0429686,0),(1.22833,0.0537046,0),(1.22781,0.0644365,0),+713 more]
  Presets = 11
  Quality = 1
  Support = -> [DatumPlane045]
  ThreadCount = 12
  Version = 1.69
  external_data = <same value as first occurrence — deduplicated (x15 in doc)>
  internal_data = <same value as first occurrence — deduplicated (x15 in doc)>
  preset_names = <blob: 3959 chars omitted>
  presets_data = <same value as first occurrence — deduplicated (x15 in doc)>
FEATURE [Part::Helix] Helix024
  Angle = 0
  AttacherType = Attacher::AttachEngine3D
  Height = 6
  LocalCoord = 0
  Pitch = 0.5
  Placement = pos=(-7,3.75,55.5) rot=(1e-06,1,0;3.14159rad)
  Radius = 1
  Style = 0
  expr: .Placement.Rotation.Axis.z = VThreadProfile019.Placement.Rotation.Axis.z
  expr: .Placement.Rotation.Axis.y = VThreadProfile019.Placement.Rotation.Axis.y
  expr: .Placement.Rotation.Axis.x = VThreadProfile019.Placement.Rotation.Axis.x
  expr: .Placement.Rotation.Angle = VThreadProfile019.Placement.Rotation.Angle
  expr: .Placement.Base.z = VThreadProfile019.Placement.Base.z
  expr: .Placement.Base.y = VThreadProfile019.Placement.Base.y
  expr: .Placement.Base.x = VThreadProfile019.Placement.Base.x
  expr: Height = VThreadProfile019.ThreadCount * VThreadProfile019.Pitch
  expr: Pitch = VThreadProfile019.Pitch
FEATURE [PartDesign::ShapeBinder] ShapeBinder020
  Placement = pos=(-7,3.75,55.5) rot=(1e-06,1,0;3.14159rad)
  Support = -> [Helix024]
  TraceSupport = false
FEATURE [PartDesign::SubtractivePipe] SubtractivePipe015
  AuxilleryCurvelinear = true
  AuxillerySpineTangent = false
  BaseFeature = -> SubtractivePipe014
  Binormal = (0,0,0)
  Mode = 2
  Placement = pos=(0,0,0) rot=(0.57735,0.57735,0.57735;4.18879rad)
  Profile = -> VThreadProfile019
  Spine = -> ShapeBinder020
  SpineTangent = false
  Transformation = 0
  Transition = 0
FEATURE [PartDesign::Plane] DatumPlane046
  AttachmentOffset = pos=(0,0,0) rot=(0,1,0;3.14159rad)
  Length = 60
  MapMode = 45
  Placement = pos=(-7,-3.75,55.5) rot=(0,1,0;3.14159rad)
  ResizeMode = 0
  Support = -> [Pocket033]
  Width = 60
FEATURE [Part::Part2DObjectPython] VThreadProfile020  # Draft 2D object (typed FeaturePython)
  Area = 5.75678
  Closed = true
  Continuity = C3
  Instructions = <same value as first occurrence — deduplicated (x15 in doc)>
  InternalOrExternal = 0
  MakeFace = true
  MapMode = 2
  MinorDiameter = 2.459
  Parameterization = 1
  Pitch = 0.5
  Placement = pos=(-7,-3.75,55.5) rot=(0,1,0;3.14159rad)
  Points = (719) [(1.22945,0.0107442,0),(1.22931,0.0214876,0),(1.22908,0.0322293,0),(1.22875,0.0429686,0),(1.22833,0.0537046,0),(1.22781,0.0644365,0),+713 more]
  Presets = 11
  Quality = 1
  Support = -> [DatumPlane046]
  ThreadCount = 12
  Version = 1.69
  external_data = <same value as first occurrence — deduplicated (x15 in doc)>
  internal_data = <same value as first occurrence — deduplicated (x15 in doc)>
  preset_names = <blob: 3959 chars omitted>
  presets_data = <same value as first occurrence — deduplicated (x15 in doc)>
FEATURE [Part::Helix] Helix025
  Angle = 0
  AttacherType = Attacher::AttachEngine3D
  Height = 6
  LocalCoord = 0
  Pitch = 0.5
  Placement = pos=(-7,-3.75,55.5) rot=(0,1,0;3.14159rad)
  Radius = 1
  Style = 0
  expr: .Placement.Rotation.Axis.z = VThreadProfile020.Placement.Rotation.Axis.z
  expr: .Placement.Rotation.Axis.y = VThreadProfile020.Placement.Rotation.Axis.y
  expr: .Placement.Rotation.Axis.x = VThreadProfile020.Placement.Rotation.Axis.x
  expr: .Placement.Rotation.Angle = VThreadProfile020.Placement.Rotation.Angle
  expr: .Placement.Base.z = VThreadProfile020.Placement.Base.z
  expr: .Placement.Base.y = VThreadProfile020.Placement.Base.y
  expr: .Placement.Base.x = VThreadProfile020.Placement.Base.x
  expr: Height = VThreadProfile020.ThreadCount * VThreadProfile020.Pitch
  expr: Pitch = VThreadProfile020.Pitch
FEATURE [PartDesign::ShapeBinder] ShapeBinder021
  Placement = pos=(-7,-3.75,55.5) rot=(0,1,0;3.14159rad)
  Support = -> [Helix025]
  TraceSupport = false
FEATURE [PartDesign::SubtractivePipe] SubtractivePipe016
  AuxilleryCurvelinear = true
  AuxillerySpineTangent = false
  BaseFeature = -> SubtractivePipe015
  Binormal = (0,0,0)
  Mode = 2
  Placement = pos=(0,0,0) rot=(0.57735,0.57735,0.57735;4.18879rad)
  Profile = -> VThreadProfile020
  Spine = -> ShapeBinder021
  SpineTangent = false
  Transformation = 0
  Transition = 0
FEATURE [PartDesign::Plane] DatumPlane047
  AttachmentOffset = pos=(0,0,0) rot=(0,1,0;3.14159rad)
  Length = 60
  MapMode = 11
  Placement = pos=(7,-3.75,55.5) rot=(-0.707107,0.707107,0;3.14159rad)
  ResizeMode = 0
  Support = -> [Pocket033]
  Width = 60
FEATURE [Part::Part2DObjectPython] VThreadProfile021  # Draft 2D object (typed FeaturePython)
  Area = 5.75678
  Closed = true
  Continuity = C3
  Instructions = <same value as first occurrence — deduplicated (x15 in doc)>
  InternalOrExternal = 0
  MakeFace = true
  MapMode = 5
  MinorDiameter = 2.459
  Parameterization = 1
  Pitch = 0.5
  Placement = pos=(7,-3.75,55.5) rot=(-0.707107,0.707107,0;3.14159rad)
  Points = (719) [(1.22945,0.0107442,0),(1.22931,0.0214876,0),(1.22908,0.0322293,0),(1.22875,0.0429686,0),(1.22833,0.0537046,0),(1.22781,0.0644365,0),+713 more]
  Presets = 11
  Quality = 1
  Support = -> [DatumPlane047]
  ThreadCount = 12
  Version = 1.69
  external_data = <same value as first occurrence — deduplicated (x15 in doc)>
  internal_data = <same value as first occurrence — deduplicated (x15 in doc)>
  preset_names = <blob: 3959 chars omitted>
  presets_data = <same value as first occurrence — deduplicated (x15 in doc)>
FEATURE [Part::Helix] Helix026
  Angle = 0
  AttacherType = Attacher::AttachEngine3D
  Height = 6
  LocalCoord = 0
  Pitch = 0.5
  Placement = pos=(7,-3.75,55.5) rot=(-0.707107,0.707107,0;3.14159rad)
  Radius = 1
  Style = 0
  expr: .Placement.Rotation.Axis.z = VThreadProfile021.Placement.Rotation.Axis.z
  expr: .Placement.Rotation.Axis.y = VThreadProfile021.Placement.Rotation.Axis.y
  expr: .Placement.Rotation.Axis.x = VThreadProfile021.Placement.Rotation.Axis.x
  expr: .Placement.Rotation.Angle = VThreadProfile021.Placement.Rotation.Angle
  expr: .Placement.Base.z = VThreadProfile021.Placement.Base.z
  expr: .Placement.Base.y = VThreadProfile021.Placement.Base.y
  expr: .Placement.Base.x = VThreadProfile021.Placement.Base.x
  expr: Height = VThreadProfile021.ThreadCount * VThreadProfile021.Pitch
  expr: Pitch = VThreadProfile021.Pitch
FEATURE [PartDesign::ShapeBinder] ShapeBinder022
  Placement = pos=(7,-3.75,55.5) rot=(-0.707107,0.707107,0;3.14159rad)
  Support = -> [Helix026]
  TraceSupport = false
FEATURE [PartDesign::SubtractivePipe] SubtractivePipe017
  AuxilleryCurvelinear = true
  AuxillerySpineTangent = false
  BaseFeature = -> SubtractivePipe016
  Binormal = (0,0,0)
  Mode = 2
  Placement = pos=(0,0,0) rot=(0.57735,0.57735,0.57735;4.18879rad)
  Profile = -> VThreadProfile021
  Spine = -> ShapeBinder022
  SpineTangent = false
  Transformation = 0
  Transition = 0
FEATURE [PartDesign::Plane] DatumPlane048
  AttachmentOffset = pos=(0,0,0) rot=(0,1,0;3.14159rad)
  Length = 60
  MapMode = 45
  Placement = pos=(7,3.75,55.5) rot=(0,1,0;3.14159rad)
  ResizeMode = 0
  Support = -> [Pocket033]
  Width = 60
FEATURE [Part::Part2DObjectPython] VThreadProfile022  # Draft 2D object (typed FeaturePython)
  Area = 5.75678
  Closed = true
  Continuity = C3
  Instructions = <same value as first occurrence — deduplicated (x15 in doc)>
  InternalOrExternal = 0
  MakeFace = true
  MapMode = 5
  MinorDiameter = 2.459
  Parameterization = 1
  Pitch = 0.5
  Placement = pos=(7,3.75,55.5) rot=(0,1,0;3.14159rad)
  Points = (719) [(1.22945,0.0107442,0),(1.22931,0.0214876,0),(1.22908,0.0322293,0),(1.22875,0.0429686,0),(1.22833,0.0537046,0),(1.22781,0.0644365,0),+713 more]
  Presets = 11
  Quality = 1
  Support = -> [DatumPlane048]
  ThreadCount = 12
  Version = 1.69
  external_data = <same value as first occurrence — deduplicated (x15 in doc)>
  internal_data = <same value as first occurrence — deduplicated (x15 in doc)>
  preset_names = <blob: 3959 chars omitted>
  presets_data = <same value as first occurrence — deduplicated (x15 in doc)>
FEATURE [Part::Helix] Helix027
  Angle = 0
  AttacherType = Attacher::AttachEngine3D
  Height = 6
  LocalCoord = 0
  Pitch = 0.5
  Placement = pos=(7,3.75,55.5) rot=(0,1,0;3.14159rad)
  Radius = 1
  Style = 0
  expr: .Placement.Rotation.Axis.z = VThreadProfile022.Placement.Rotation.Axis.z
  expr: .Placement.Rotation.Axis.y = VThreadProfile022.Placement.Rotation.Axis.y
  expr: .Placement.Rotation.Axis.x = VThreadProfile022.Placement.Rotation.Axis.x
  expr: .Placement.Rotation.Angle = VThreadProfile022.Placement.Rotation.Angle
  expr: .Placement.Base.z = VThreadProfile022.Placement.Base.z
  expr: .Placement.Base.y = VThreadProfile022.Placement.Base.y
  expr: .Placement.Base.x = VThreadProfile022.Placement.Base.x
  expr: Height = VThreadProfile022.ThreadCount * VThreadProfile022.Pitch
  expr: Pitch = VThreadProfile022.Pitch
FEATURE [PartDesign::ShapeBinder] ShapeBinder023
  Placement = pos=(7,3.75,55.5) rot=(0,1,0;3.14159rad)
  Support = -> [Helix027]
  TraceSupport = false
FEATURE [PartDesign::SubtractivePipe] SubtractivePipe018
  AuxilleryCurvelinear = true
  AuxillerySpineTangent = false
  BaseFeature = -> SubtractivePipe017
  Binormal = (0,0,0)
  Mode = 2
  Placement = pos=(0,0,0) rot=(0.57735,0.57735,0.57735;4.18879rad)
  Profile = -> VThreadProfile022
  Spine = -> ShapeBinder023
  SpineTangent = false
  Transformation = 0
  Transition = 0
FEATURE [PartDesign::Plane] DatumPlane049
  Length = 60.0307
  MapMode = 11
  Placement = pos=(1.05068e-07,4.93397e-08,48.7004) rot=(0.000101,0.000234,-1;1.5708rad)
  ResizeMode = 0
  Support = -> [SubtractivePipe014]
  Width = 60.0144
FEATURE [Sketcher::SketchObject] Sketch028
  FullyConstrained = true
  MapMode = 5
  Placement = pos=(1.05068e-07,4.93397e-08,48.7004) rot=(0.000101,0.000234,-1;1.5708rad)
  Support = -> [DatumPlane049]
  sketch-geometry (1):
    g0: Circle CenterX=0 CenterY=0 CenterZ=0 NormalX=0 NormalY=0 NormalZ=1 AngleXU=0 Radius=2.1
  constraints (2):
    c: Coincident(g0,g-1)
    c: Radius(g0) = 2.1
FEATURE [PartDesign::Pocket] Pocket034
  BaseFeature = -> SubtractivePipe018
  Length = 2.3
  Length2 = 100
  Placement = pos=(0,0,0) rot=(0.57735,0.57735,0.57735;4.18879rad)
  Profile = -> Sketch028
  Type = 0
FEATURE [PartDesign::SubShapeBinder] Binder001
  BindMode = 0
  ClaimChildren = false
  Context = -> Part [Body004.Binder001.]
  Fuse = false
  MakeFace = true
  PartialLoad = false
  Relative = true
  Support = -> [Body003[Pocket033.Face212]]
  _Version = 2
FEATURE [Sketcher::SketchObject] Sketch019
  ExternalGeometry = -> [Binder001]
  FullyConstrained = false
  MapMode = 5
  Placement = pos=(6e-15,-2.9e-14,26) rot=(0,1,0;3.14159rad)
  sketch-geometry (2):
    g0: Circle CenterX=6 CenterY=-3 CenterZ=0 NormalX=0 NormalY=0 NormalZ=1 AngleXU=0 Radius=1
    g1: Circle CenterX=6 CenterY=-3 CenterZ=0 NormalX=0 NormalY=0 NormalZ=1 AngleXU=0 Radius=0.9
  constraints (3):
    c: Coincident(g1,g0)
    c: Radius(g0) = 1
    c: Radius(g1) = 0.9
FEATURE [PartDesign::Pad] Pad004
  Direction = (1,1,1)
  Length = 10
  Length2 = 100
  Placement = pos=(6e-15,-2.9e-14,26) rot=(0,1,0;3.14159rad)
  Profile = -> Sketch019
  Type = 0
FEATURE [PartDesign::Body] Body004  label="spacer1"
  Group = -> [Sketch019,Binder001,Pad004]
  Origin = -> Origin005
  Tip = -> Pad004
FEATURE [PartDesign::FeatureBase] Clone
  BaseFeature = -> Body004
FEATURE [PartDesign::Body] Body005  label="spacer2"
  BaseFeature = -> Body004
  Group = -> [Clone]
  Origin = -> Origin006
  Placement = pos=(12,0,0) rot=(0,0,1;0rad)
  Tip = -> Clone
FEATURE [PartDesign::FeatureBase] Clone001
  BaseFeature = -> Body004
FEATURE [PartDesign::Body] Body006  label="spacer3"
  BaseFeature = -> Body004
  Group = -> [Clone001]
  Origin = -> Origin007
  Placement = pos=(12,6,0) rot=(0,0,1;0rad)
  Tip = -> Clone001
FEATURE [PartDesign::FeatureBase] Clone002
  BaseFeature = -> Body004
FEATURE [PartDesign::Body] Body007  label="spacer4"
  BaseFeature = -> Body004
  Group = -> [Clone002]
  Origin = -> Origin008
  Placement = pos=(0,6,0) rot=(0,0,1;0rad)
  Tip = -> Clone002
FEATURE [PartDesign::Plane] DatumPlane050
  Length = 93.1886
  MapMode = 3
  Placement = pos=(0,0,0) rot=(0,-1,0;1.5708rad)
  ResizeMode = 0
  Support = -> [Z_Axis004]
  Width = 62.6886
FEATURE [Sketcher::SketchObject] Sketch029
  ExternalGeometry = -> [Pocket034]
  FullyConstrained = true
  MapMode = 5
  Placement = pos=(0,0,0) rot=(0,-1,0;1.5708rad)
  Support = -> [DatumPlane050]
  sketch-geometry (3):
    g0: LineSegment StartX=45.2 StartY=0.5 StartZ=0 EndX=46.7 EndY=0.5 EndZ=0
    g1: LineSegment StartX=46.7 StartY=0.5 StartZ=0 EndX=46.7 EndY=2 EndZ=0
    g2: LineSegment StartX=46.7 StartY=2 StartZ=0 EndX=45.2 EndY=0.5 EndZ=0
  constraints (9):
    c: Horizontal(g0)
    c: Coincident(g0,g1)
    c: Vertical(g1)
    c: Coincident(g1,g2)
    c: Coincident(g2,g0)
    c: Angle(g0,g2) = 0.785398
    c: Distance(g1,g-1) = 2
    c: Distance(g0,g-1) = 0.5
    c: DistanceX(g0) = 46.7
FEATURE [PartDesign::Groove] Groove
  Angle = 360
  Axis = (-2e-16,3e-16,1)
  Base = (0,0,0)
  BaseFeature = -> Pocket034
  Placement = pos=(0,0,0) rot=(0.57735,0.57735,0.57735;4.18879rad)
  Profile = -> Sketch029
  ReferenceAxis = -> Sketch029 [H_Axis]
  Reversed = true
FEATURE [PartDesign::Body] Body003  label="case"
  Group = -> [DatumPlane010,Sketch009,Revolution002,DatumPlane011,Sketch010,Pocket010,DatumPlane012,Sketch011,Pocket011,DatumPlane013,Sketch012,Pocket012,DatumPlane014,Sketch013,DatumPlane015,Sketch014,Pocket014,Sketch015,Pocket015,Pocket016,DatumPlane017,Sketch017,Pocket019,Binder,Sketch016,DatumPlane041,Pocket032,Sketch027,Pocket033,DatumPlane042,VThreadProfile016,ShapeBinder017,SubtractivePipe012,+30 more]
  Origin = -> Origin004
  Tip = -> Groove
FEATURE [PartDesign::Plane] DatumPlane051
  Length = 60
  MapMode = 5
  Placement = pos=(2.1e-15,-1.8e-15,9) rot=(0,1,0;3.14159rad)
  ResizeMode = 0
  Support = -> [AdditivePipe001]
  Width = 60
FEATURE [Sketcher::SketchObject] Sketch030
  FullyConstrained = true
  MapMode = 5
  Placement = pos=(2.1e-15,-1.8e-15,9) rot=(0,1,0;3.14159rad)
  Support = -> [DatumPlane051]
  sketch-geometry (1):
    g0: Circle CenterX=0 CenterY=0 CenterZ=0 NormalX=0 NormalY=0 NormalZ=1 AngleXU=0 Radius=1
  constraints (2):
    c: Coincident(g0,g-1)
    c: Radius(g0) = 1
FEATURE [PartDesign::Pocket] Pocket036
  BaseFeature = -> AdditivePipe001
  Length = 5
  Length2 = 100
  Placement = pos=(0,0,0) rot=(0.57735,0.57735,0.57735;4.18879rad)
  Profile = -> AdditivePipe001 [Face20]
  Type = 1
FEATURE [PartDesign::Body] Body  label="nozzle"
  Group = -> [DatumPlane,Sketch,Revolution,DatumPlane001,Sketch001,Pocket,VThreadProfile001,ShapeBinder002,AdditivePipe001,DatumPlane051,Sketch030,Pocket036]
  Origin = -> Origin001
  Placement = pos=(0,0,0) rot=(0,0,-1;3.14159rad)
  Tip = -> Pocket036
FEATURE [PartDesign::Plane] DatumPlane002
  Length = 60.0034
  MapMode = 11
  Placement = pos=(-2.0069e-09,1.2e-15,13) rot=(2.2e-05,-2.2e-05,1;1.5708rad)
  ResizeMode = 0
  Support = -> [Pocket036]
  Width = 60.0003
FEATURE [Sketcher::SketchObject] Sketch002
  ExternalGeometry = -> [DatumPlane002]
  FullyConstrained = true
  MapMode = 5
  Placement = pos=(0,0,0) rot=(0.57735,0.57735,0.57735;4.18879rad)
  Support = -> [DatumPlane003]
  sketch-geometry (44):
    g0: LineSegment StartX=18.5 StartY=2.5 StartZ=0 EndX=18.5 EndY=4 EndZ=0
    g1: LineSegment StartX=18.5 StartY=4 StartZ=0 EndX=20 EndY=4 EndZ=0
    g2: LineSegment StartX=20 StartY=4 StartZ=0 EndX=20 EndY=1.1 EndZ=0
    g3: LineSegment StartX=20 StartY=1.1 StartZ=0 EndX=22 EndY=1.1 EndZ=0
    g4: LineSegment StartX=22 StartY=1.1 StartZ=0 EndX=22 EndY=1.75 EndZ=0
    g5: LineSegment StartX=22 StartY=1.75 StartZ=0 EndX=27.5 EndY=1.75 EndZ=0
    g6: LineSegment StartX=27.5 StartY=1.75 StartZ=0 EndX=27.5 EndY=4 EndZ=0
    g7: LineSegment StartX=27.5 StartY=4 StartZ=0 EndX=28 EndY=4 EndZ=0
    g8: LineSegment StartX=28 StartY=4 StartZ=0 EndX=28 EndY=1.75 EndZ=0
    g9: LineSegment StartX=28 StartY=1.75 StartZ=0 EndX=28.8 EndY=1.75 EndZ=0
    g10: LineSegment StartX=28.8 StartY=1.75 StartZ=0 EndX=28.8 EndY=4 EndZ=0
    g11: LineSegment StartX=28.8 StartY=4 StartZ=0 EndX=29.3 EndY=4 EndZ=0
    g12: LineSegment StartX=29.3 StartY=4 StartZ=0 EndX=29.3 EndY=1.75 EndZ=0
    g13: LineSegment StartX=29.3 StartY=1.75 StartZ=0 EndX=30.1 EndY=1.75 EndZ=0
    g14: LineSegment StartX=30.1 StartY=1.75 StartZ=0 EndX=30.1 EndY=4 EndZ=0
    g15: LineSegment StartX=30.1 StartY=4 StartZ=0 EndX=30.6 EndY=4 EndZ=0
    g16: LineSegment StartX=30.6 StartY=4 StartZ=0 EndX=30.6 EndY=1.75 EndZ=0
    g17: LineSegment StartX=30.6 StartY=1.75 StartZ=0 EndX=31.4 EndY=1.75 EndZ=0
    g18: LineSegment StartX=31.4 StartY=1.75 StartZ=0 EndX=31.4 EndY=4 EndZ=0
    g19: LineSegment StartX=31.4 StartY=4 StartZ=0 EndX=31.9 EndY=4 EndZ=0
    g20: LineSegment StartX=31.9 StartY=4 StartZ=0 EndX=31.9 EndY=1.75 EndZ=0
    g21: LineSegment StartX=31.9 StartY=1.75 StartZ=0 EndX=32.7 EndY=1.75 EndZ=0
    g22: LineSegment StartX=32.7 StartY=1.75 StartZ=0 EndX=32.7 EndY=4 EndZ=0
    g23: LineSegment StartX=32.7 StartY=4 StartZ=0 EndX=33.2 EndY=4 EndZ=0
    g24: LineSegment StartX=33.2 StartY=4 StartZ=0 EndX=33.2 EndY=1.75 EndZ=0
    g25: LineSegment StartX=33.2 StartY=1.75 StartZ=0 EndX=34 EndY=1.75 EndZ=0
    g26: LineSegment StartX=34 StartY=1.75 StartZ=0 EndX=34 EndY=4 EndZ=0
    g27: LineSegment StartX=34 StartY=4 StartZ=0 EndX=34.5 EndY=4 EndZ=0
    g28: LineSegment StartX=34.5 StartY=4 StartZ=0 EndX=34.5 EndY=1.75 EndZ=0
    g29: LineSegment StartX=34.5 StartY=1.75 StartZ=0 EndX=35.3 EndY=1.75 EndZ=0
    g30: LineSegment StartX=35.3 StartY=1.75 StartZ=0 EndX=35.3 EndY=4 EndZ=0
    g31: LineSegment StartX=35.3 StartY=4 StartZ=0 EndX=35.8 EndY=4 EndZ=0
    g32: LineSegment StartX=35.8 StartY=4 StartZ=0 EndX=35.8 EndY=1.75 EndZ=0
    g33: LineSegment StartX=35.8 StartY=1.75 StartZ=0 EndX=36.6 EndY=1.75 EndZ=0
    g34: LineSegment StartX=36.6 StartY=1.75 StartZ=0 EndX=36.6 EndY=3 EndZ=0
    g35: LineSegment StartX=36.6 StartY=3 StartZ=0 EndX=37.1 EndY=3 EndZ=0
    g36: LineSegment StartX=37.1 StartY=3 StartZ=0 EndX=37.1 EndY=1.75 EndZ=0
    g37: LineSegment StartX=37.1 StartY=1.75 StartZ=0 EndX=42.5 EndY=1.75 EndZ=0
    g38: LineSegment StartX=42.5 StartY=1.75 StartZ=0 EndX=42.5 EndY=1.1 EndZ=0
    g39: LineSegment StartX=42.5 StartY=1.1 StartZ=0 EndX=44.5 EndY=1.1 EndZ=0
    g40: LineSegment StartX=44.5 StartY=1.1 StartZ=0 EndX=44.5 EndY=1 EndZ=0
    g41: LineSegment StartX=44.5 StartY=1 StartZ=0 EndX=17.5 EndY=1 EndZ=0
    g42: LineSegment StartX=17.5 StartY=2.5 StartZ=0 EndX=18.5 EndY=2.5 EndZ=0
    g43: LineSegment StartX=17.5 StartY=1 StartZ=0 EndX=17.5 EndY=2.5 EndZ=0
  constraints (132):
    c: Vertical(g0)
    c: Coincident(g0,g1)
    c: Horizontal(g1)
    c: Coincident(g1,g2)
    c: Vertical(g2)
    c: Coincident(g2,g3)
    c: Horizontal(g3)
    c: Vertical(g4)
    c: Coincident(g4,g5)
    c: Horizontal(g5)
    c: Coincident(g5,g6)
    c: Vertical(g6)
    c: Coincident(g6,g7)
    c: Coincident(g7,g8)
    c: Vertical(g8)
    c: Coincident(g8,g9)
    c: Coincident(g9,g10)
    c: Vertical(g10)
    c: Coincident(g10,g11)
    c: Coincident(g11,g12)
    c: Vertical(g12)
    c: Coincident(g12,g13)
    c: Coincident(g13,g14)
    c: Vertical(g14)
    c: Coincident(g14,g15)
    c: Coincident(g15,g16)
    c: Vertical(g16)
    c: Coincident(g16,g17)
    c: Coincident(g17,g18)
    c: Vertical(g18)
    c: Coincident(g18,g19)
    c: Coincident(g19,g20)
    c: Vertical(g20)
    c: Coincident(g20,g21)
    c: Coincident(g21,g22)
    c: Vertical(g22)
    c: Coincident(g22,g23)
    c: Coincident(g23,g24)
    c: Vertical(g24)
    c: Coincident(g24,g25)
    c: Coincident(g25,g26)
    c: Vertical(g26)
    c: Coincident(g26,g27)
    c: Coincident(g27,g28)
    c: Vertical(g28)
    c: Coincident(g28,g29)
    c: Coincident(g29,g30)
    c: Vertical(g30)
    c: Coincident(g30,g31)
    c: Coincident(g31,g32)
    c: Vertical(g32)
    c: Coincident(g32,g33)
    c: Coincident(g33,g34)
    c: Vertical(g34)
    c: Coincident(g34,g35)
    c: Horizontal(g35)
    c: Coincident(g35,g36)
    c: Vertical(g36)
    c: Coincident(g36,g37)
    c: Coincident(g37,g38)
    c: Coincident(g38,g39)
    c: Horizontal(g39)
    c: Coincident(g39,g40)
    c: Coincident(g40,g41)
    c: Horizontal(g41)
    c: Horizontal(g7)
    c: Horizontal(g11)
    c: Horizontal(g15)
    c: Horizontal(g19)
    c: Horizontal(g23)
    c: Horizontal(g27)
    c: Horizontal(g31)
    c: Horizontal(g7,g11)
    c: Horizontal(g11,g15)
    c: Horizontal(g15,g19)
    c: Horizontal(g19,g23)
    c: Horizontal(g23,g27)
    c: Horizontal(g27,g31)
    c: Horizontal(g9)
    c: Horizontal(g13)
    c: Horizontal(g17)
    c: Horizontal(g21)
    c: Horizontal(g25)
    c: Horizontal(g29)
    c: Horizontal(g33)
    c: Horizontal(g37)
    c: Vertical(g38)
    c: Horizontal(g5,g9)
    c: Horizontal(g9,g13)
    c: Horizontal(g13,g17)
    c: Horizontal(g17,g21)
    c: Horizontal(g21,g25)
    c: Horizontal(g25,g29)
    c: Horizontal(g29,g33)
    c: Horizontal(g33,g37)
    c: Equal(g7,g11)
    c: Equal(g11,g15)
    c: Equal(g15,g19)
    c: Equal(g19,g23)
    c: Equal(g23,g27)
    c: Equal(g27,g31)
    c: Equal(g31,g35)
    c: Equal(g9,g13)
    c: Equal(g13,g17)
    c: Equal(g17,g21)
    c: Equal(g21,g25)
    c: Equal(g25,g29)
    c: Equal(g29,g33)
    c: Distance(g9) = 0.8
    c: Distance(g35) = 0.5
    c: Distance(g6,g-1) = 4
    c: Horizontal(g38,g4)
    c: Coincident(g3,g4)
    c: Distance(g3,g-1) = 1.1
    c: Distance(g4,g-1) = 1.75
    c: Vertical(g40)
    c: Distance(g1) = 1.5
    c: Distance(g39,g0) = 26
    c: Distance(g39) = 2
    c: Distance(g35,g-1) = 3
    c: Distance(g41,g-1) = 1
    c: Distance(g37,g4) = 20.5
    c: Distance(g5) = 5.5
    c: Distance(g1,g-1) = 4
    c: Horizontal(g42)
    c: Coincident(g0,g42)
    c: Distance(g0,g-1) = 2.5
    c: Distance(g42) = 1
    c: Distance(g0,g-2) = 18.5
    c: Coincident(g43,g41)
    c: Coincident(g43,g42)
    c: Vertical(g43)
FEATURE [PartDesign::Revolution] Revolution001
  Angle = 360
  Axis = (-4e-16,4e-16,1)
  Base = (0,0,0)
  Placement = pos=(0,0,0) rot=(0.57735,0.57735,0.57735;4.18879rad)
  Profile = -> Sketch002
  ReferenceAxis = -> Sketch002 [H_Axis]
FEATURE [Sketcher::SketchObject] Sketch003
  FullyConstrained = true
  MapMode = 5
  Placement = pos=(-2.0069e-09,1.2e-15,13) rot=(2.2e-05,-2.2e-05,1;1.5708rad)
  Support = -> [DatumPlane002]
  sketch-geometry (8):
    g0: LineSegment StartX=3.5 StartY=2.02073 StartZ=0 EndX=0 EndY=4.04145 EndZ=0
    g1: LineSegment StartX=0 StartY=4.04145 StartZ=0 EndX=-3.5 EndY=2.02073 EndZ=0
    g2: LineSegment StartX=-3.5 StartY=2.02073 StartZ=0 EndX=-3.5 EndY=-2.02073 EndZ=0
    g3: LineSegment StartX=-3.5 StartY=-2.02073 StartZ=0 EndX=-1.8e-15 EndY=-4.04145 EndZ=0
    g4: LineSegment StartX=-1.8e-15 StartY=-4.04145 StartZ=0 EndX=3.5 EndY=-2.02073 EndZ=0
    g5: LineSegment StartX=3.5 StartY=-2.02073 StartZ=0 EndX=3.5 EndY=2.02073 EndZ=0
    g6: Circle CenterX=0 CenterY=0 CenterZ=0 NormalX=0 NormalY=0 NormalZ=1 AngleXU=0 Radius=4.04145
    g7: Circle CenterX=0 CenterY=0 CenterZ=0 NormalX=0 NormalY=0 NormalZ=1 AngleXU=0 Radius=6
  constraints (18):
    c: Coincident(g0,g1)
    c: Coincident(g1,g2)
    c: Coincident(g2,g3)
    c: Coincident(g3,g4)
    c: Coincident(g4,g5)
    c: Coincident(g5,g0)
    c: Equal(g0, g1-g5) x5
    c: PointOnObject(g0,g6)
    c: PointOnObject(g1,g6)
    c: PointOnObject(g2,g6)
    c: PointOnObject(g3,g6)
    c: PointOnObject(g4,g6)
    c: PointOnObject(g5,g6)
    c: Coincident(g6,g-1)
    c: Perpendicular(g-1,g2)
    c: Distance(g1,g3) = 7
    c: Coincident(g7,g-1)
    c: Radius(g7) = 6
FEATURE [PartDesign::Pocket] Pocket001
  BaseFeature = -> Revolution001
  Length = 0
  Length2 = 100
  Placement = pos=(0,0,0) rot=(0.57735,0.57735,0.57735;4.18879rad)
  Profile = -> Sketch003
  Reversed = true
  Type = 3
  UpToFace = -> Revolution001 [Face7]
FEATURE [PartDesign::Plane] DatumPlane052
  Length = 60
  MapMode = 5
  Placement = pos=(-7.8e-15,-1.9e-15,17.5) rot=(0,1,0;3.14159rad)
  ResizeMode = 0
  Support = -> [Pocket001]
  Width = 60
FEATURE [Part::Part2DObjectPython] VThreadProfile023  # Draft 2D object (typed FeaturePython)
  Area = 21.5648
  Closed = true
  Continuity = C3
  Instructions = <same value as first occurrence — deduplicated (x15 in doc)>
  InternalOrExternal = 1
  MakeFace = true
  MapMode = 5
  MinorDiameter = 4.773
  Parameterization = 1
  Pitch = 1
  Placement = pos=(-7.8e-15,-1.9e-15,17.5) rot=(0,1,0;3.14159rad)
  Points = (719) [(2.38406,0.0208343,0),(2.38153,0.0416275,0),(2.3789,0.0623805,0),(2.37618,0.0830937,0),(2.37336,0.103767,0),(2.37042,0.124402,0),(2.36737,0.144997,0),+712 more]
  Presets = 16
  Quality = 1
  Support = -> [DatumPlane052]
  ThreadCount = 4.5
  Version = 1.69
  external_data = <same value as first occurrence — deduplicated (x15 in doc)>
  internal_data = <same value as first occurrence — deduplicated (x15 in doc)>
  preset_names = <blob: 3959 chars omitted>
  presets_data = <same value as first occurrence — deduplicated (x15 in doc)>
FEATURE [Part::Helix] Helix028
  Angle = 0
  AttacherType = Attacher::AttachEngine3D
  Height = 4.5
  LocalCoord = 0
  Pitch = 1
  Placement = pos=(-7.8e-15,-1.9e-15,17.5) rot=(0,1,0;3.14159rad)
  Radius = 1
  Style = 0
  expr: .Placement.Rotation.Axis.z = VThreadProfile023.Placement.Rotation.Axis.z
  expr: .Placement.Rotation.Axis.y = VThreadProfile023.Placement.Rotation.Axis.y
  expr: .Placement.Rotation.Axis.x = VThreadProfile023.Placement.Rotation.Axis.x
  expr: .Placement.Rotation.Angle = VThreadProfile023.Placement.Rotation.Angle
  expr: .Placement.Base.z = VThreadProfile023.Placement.Base.z
  expr: .Placement.Base.y = VThreadProfile023.Placement.Base.y
  expr: .Placement.Base.x = VThreadProfile023.Placement.Base.x
  expr: Height = VThreadProfile023.ThreadCount * VThreadProfile023.Pitch
  expr: Pitch = VThreadProfile023.Pitch
FEATURE [PartDesign::ShapeBinder] ShapeBinder024
  Placement = pos=(-7.8e-15,-1.9e-15,17.5) rot=(0,1,0;3.14159rad)
  Support = -> [Helix028]
  TraceSupport = false
FEATURE [PartDesign::AdditivePipe] AdditivePipe004
  AuxilleryCurvelinear = true
  AuxillerySpineTangent = false
  BaseFeature = -> Pocket001
  Binormal = (0,0,0)
  Mode = 2
  Placement = pos=(0,0,0) rot=(0.57735,0.57735,0.57735;4.18879rad)
  Profile = -> VThreadProfile023
  Spine = -> ShapeBinder024
  SpineTangent = false
  Transformation = 0
  Transition = 0
FEATURE [PartDesign::Pocket] Pocket037
  BaseFeature = -> AdditivePipe004
  Length = 5
  Length2 = 100
  Placement = pos=(0,0,0) rot=(0.57735,0.57735,0.57735;4.18879rad)
  Profile = -> AdditivePipe004 [Face70]
  Type = 1
FEATURE [PartDesign::Body] Body001  label="heatbreak standard"
  Group = -> [DatumPlane002,DatumPlane003,Sketch002,Revolution001,Sketch003,Pocket001,DatumPlane052,VThreadProfile023,ShapeBinder024,AdditivePipe004,Pocket037]
  Origin = -> Origin002
  Tip = -> Pocket037
FEATURE [PartDesign::Pocket] Pocket038
  BaseFeature = -> Pocket008
  Length = 5
  Length2 = 100
  Placement = pos=(0,0,18.5) rot=(0,1,0;3.14159rad)
  Profile = -> Sketch005 [Edge1]
  Type = 1
FEATURE [PartDesign::Pocket] Pocket039
  BaseFeature = -> Pocket038
  Length = 5
  Length2 = 100
  Placement = pos=(0,0,18.5) rot=(0,1,0;3.14159rad)
  Profile = -> Pocket038 [Face23]
  Type = 1
FEATURE [Part::Part2DObjectPython] VThreadProfile024  # Draft 2D object (typed FeaturePython)
  Area = 5.75678
  Closed = true
  Continuity = C3
  Instructions = <same value as first occurrence — deduplicated (x15 in doc)>
  InternalOrExternal = 0
  MakeFace = true
  MapMode = 45
  MinorDiameter = 2.459
  Parameterization = 1
  Pitch = 0.5
  Placement = pos=(10,-3,14) rot=(-0.57735,0.57735,0.57735;4.18879rad)
  Points = (719) [(1.22945,0.0107442,0),(1.22931,0.0214876,0),(1.22908,0.0322293,0),(1.22875,0.0429686,0),(1.22833,0.0537046,0),(1.22781,0.0644365,0),+713 more]
  Presets = 11
  Quality = 1
  Support = -> [Pocket039]
  ThreadCount = 14
  Version = 1.69
  external_data = <same value as first occurrence — deduplicated (x15 in doc)>
  internal_data = <same value as first occurrence — deduplicated (x15 in doc)>
  preset_names = <blob: 3959 chars omitted>
  presets_data = <same value as first occurrence — deduplicated (x15 in doc)>
FEATURE [Part::Helix] Helix029
  Angle = 0
  AttacherType = Attacher::AttachEngine3D
  Height = 7
  LocalCoord = 0
  Pitch = 0.5
  Placement = pos=(10,-3,14) rot=(-0.57735,0.57735,0.57735;4.18879rad)
  Radius = 1
  Style = 0
  expr: .Placement.Rotation.Axis.z = VThreadProfile024.Placement.Rotation.Axis.z
  expr: .Placement.Rotation.Axis.y = VThreadProfile024.Placement.Rotation.Axis.y
  expr: .Placement.Rotation.Axis.x = VThreadProfile024.Placement.Rotation.Axis.x
  expr: .Placement.Rotation.Angle = VThreadProfile024.Placement.Rotation.Angle
  expr: .Placement.Base.z = VThreadProfile024.Placement.Base.z
  expr: .Placement.Base.y = VThreadProfile024.Placement.Base.y
  expr: .Placement.Base.x = VThreadProfile024.Placement.Base.x
  expr: Height = VThreadProfile024.ThreadCount * VThreadProfile024.Pitch
  expr: Pitch = VThreadProfile024.Pitch
FEATURE [PartDesign::ShapeBinder] ShapeBinder025
  Placement = pos=(10,-3,14) rot=(-0.57735,0.57735,0.57735;4.18879rad)
  Support = -> [Helix029]
  TraceSupport = false
FEATURE [PartDesign::SubtractivePipe] SubtractivePipe
  AuxilleryCurvelinear = true
  AuxillerySpineTangent = false
  BaseFeature = -> Pocket039
  Binormal = (0,0,0)
  Mode = 2
  Placement = pos=(0,0,18.5) rot=(0,1,0;3.14159rad)
  Profile = -> VThreadProfile024
  Spine = -> ShapeBinder025
  SpineTangent = false
  Transformation = 0
  Transition = 0
FEATURE [Part::Part2DObjectPython] VThreadProfile025  # Draft 2D object (typed FeaturePython)
  Area = 5.75678
  Closed = true
  Continuity = C3
  Instructions = <same value as first occurrence — deduplicated (x15 in doc)>
  InternalOrExternal = 0
  MakeFace = true
  MapMode = 45
  MinorDiameter = 2.459
  Parameterization = 1
  Pitch = 0.5
  Placement = pos=(-5.6e-15,-9.9,18.5) rot=(0,1,0;3.14159rad)
  Points = (719) [(1.22945,0.0107442,0),(1.22931,0.0214876,0),(1.22908,0.0322293,0),(1.22875,0.0429686,0),(1.22833,0.0537046,0),(1.22781,0.0644365,0),+713 more]
  Presets = 11
  Quality = 1
  Support = -> [SubtractivePipe]
  ThreadCount = 8
  Version = 1.69
  external_data = <same value as first occurrence — deduplicated (x15 in doc)>
  internal_data = <same value as first occurrence — deduplicated (x15 in doc)>
  preset_names = <blob: 3959 chars omitted>
  presets_data = <same value as first occurrence — deduplicated (x15 in doc)>
FEATURE [Part::Helix] Helix030
  Angle = 0
  AttacherType = Attacher::AttachEngine3D
  Height = 4
  LocalCoord = 0
  Pitch = 0.5
  Placement = pos=(-5.6e-15,-9.9,18.5) rot=(0,1,0;3.14159rad)
  Radius = 1
  Style = 0
  expr: .Placement.Rotation.Axis.z = VThreadProfile025.Placement.Rotation.Axis.z
  expr: .Placement.Rotation.Axis.y = VThreadProfile025.Placement.Rotation.Axis.y
  expr: .Placement.Rotation.Axis.x = VThreadProfile025.Placement.Rotation.Axis.x
  expr: .Placement.Rotation.Angle = VThreadProfile025.Placement.Rotation.Angle
  expr: .Placement.Base.z = VThreadProfile025.Placement.Base.z
  expr: .Placement.Base.y = VThreadProfile025.Placement.Base.y
  expr: .Placement.Base.x = VThreadProfile025.Placement.Base.x
  expr: Height = VThreadProfile025.ThreadCount * VThreadProfile025.Pitch
  expr: Pitch = VThreadProfile025.Pitch
FEATURE [PartDesign::ShapeBinder] ShapeBinder026
  Placement = pos=(-5.6e-15,-9.9,18.5) rot=(0,1,0;3.14159rad)
  Support = -> [Helix030]
  TraceSupport = false
FEATURE [PartDesign::SubtractivePipe] SubtractivePipe019
  AuxilleryCurvelinear = true
  AuxillerySpineTangent = false
  BaseFeature = -> SubtractivePipe
  Binormal = (0,0,0)
  Mode = 2
  Placement = pos=(0,0,18.5) rot=(0,1,0;3.14159rad)
  Profile = -> VThreadProfile025
  Spine = -> ShapeBinder026 [Edge1,Edge2,Edge3,Edge4,Edge5,Edge6,Edge7,Edge8]
  SpineTangent = false
  Transformation = 0
  Transition = 0
FEATURE [Part::Part2DObjectPython] VThreadProfile026  # Draft 2D object (typed FeaturePython)
  Area = 23.018
  Closed = true
  Continuity = C3
  Instructions = <same value as first occurrence — deduplicated (x15 in doc)>
  InternalOrExternal = 0
  MakeFace = true
  MapMode = 45
  MinorDiameter = 4.917
  Parameterization = 1
  Pitch = 1
  Placement = pos=(-1.09e-14,1e-16,18.5) rot=(0,1,0;3.14159rad)
  Points = (719) [(2.45841,0.021484,0),(2.45812,0.0429664,0),(2.45766,0.0644455,0),(2.457,0.0859197,0),(2.45615,0.107387,0),(2.45512,0.128847,0),(2.4539,0.150296,0),+712 more]
  Presets = 16
  Quality = 1
  Support = -> [SubtractivePipe019]
  ThreadCount = 11
  Version = 1.69
  external_data = <same value as first occurrence — deduplicated (x15 in doc)>
  internal_data = <same value as first occurrence — deduplicated (x15 in doc)>
  preset_names = <blob: 3959 chars omitted>
  presets_data = <same value as first occurrence — deduplicated (x15 in doc)>
FEATURE [Part::Helix] Helix031
  Angle = 0
  AttacherType = Attacher::AttachEngine3D
  Height = 11
  LocalCoord = 0
  Pitch = 1
  Placement = pos=(-1.09e-14,1e-16,18.5) rot=(0,1,0;3.14159rad)
  Radius = 1
  Style = 0
  expr: .Placement.Rotation.Axis.z = VThreadProfile026.Placement.Rotation.Axis.z
  expr: .Placement.Rotation.Axis.y = VThreadProfile026.Placement.Rotation.Axis.y
  expr: .Placement.Rotation.Axis.x = VThreadProfile026.Placement.Rotation.Axis.x
  expr: .Placement.Rotation.Angle = VThreadProfile026.Placement.Rotation.Angle
  expr: .Placement.Base.z = VThreadProfile026.Placement.Base.z
  expr: .Placement.Base.y = VThreadProfile026.Placement.Base.y
  expr: .Placement.Base.x = VThreadProfile026.Placement.Base.x
  expr: Height = VThreadProfile026.ThreadCount * VThreadProfile026.Pitch
  expr: Pitch = VThreadProfile026.Pitch
FEATURE [PartDesign::ShapeBinder] ShapeBinder027
  Placement = pos=(-1.09e-14,1e-16,18.5) rot=(0,1,0;3.14159rad)
  Support = -> [Helix031]
  TraceSupport = false
FEATURE [PartDesign::SubtractivePipe] SubtractivePipe020
  AuxilleryCurvelinear = true
  AuxillerySpineTangent = false
  BaseFeature = -> SubtractivePipe019
  Binormal = (0,0,0)
  Mode = 2
  Placement = pos=(0,0,18.5) rot=(0,1,0;3.14159rad)
  Profile = -> VThreadProfile026
  Spine = -> ShapeBinder027 [Edge1,Edge2,Edge3,Edge4,Edge5,Edge6,Edge7,Edge8,Edge9,Edge10,Edge11]
  SpineTangent = false
  Transformation = 0
  Transition = 0
FEATURE [Part::Part2DObjectPython] VThreadProfile027  # Draft 2D object (typed FeaturePython)
  Area = 5.75678
  Closed = true
  Continuity = C3
  Instructions = <same value as first occurrence — deduplicated (x15 in doc)>
  InternalOrExternal = 0
  MakeFace = true
  MapMode = 45
  MinorDiameter = 2.459
  Parameterization = 1
  Pitch = 0.5
  Placement = pos=(-4,-5,8.5) rot=(0,0,1;2e-06rad)
  Points = (719) [(1.22945,0.0107442,0),(1.22931,0.0214876,0),(1.22908,0.0322293,0),(1.22875,0.0429686,0),(1.22833,0.0537046,0),(1.22781,0.0644365,0),+713 more]
  Presets = 11
  Quality = 1
  Support = -> [SubtractivePipe020]
  ThreadCount = 14
  Version = 1.69
  external_data = <same value as first occurrence — deduplicated (x15 in doc)>
  internal_data = <same value as first occurrence — deduplicated (x15 in doc)>
  preset_names = <blob: 3959 chars omitted>
  presets_data = <same value as first occurrence — deduplicated (x15 in doc)>
FEATURE [Part::Helix] Helix032
  Angle = 0
  AttacherType = Attacher::AttachEngine3D
  Height = 7
  LocalCoord = 0
  Pitch = 0.5
  Placement = pos=(-4,-5,8.5) rot=(0,0,1;2e-06rad)
  Radius = 1
  Style = 0
  expr: .Placement.Rotation.Axis.z = VThreadProfile027.Placement.Rotation.Axis.z
  expr: .Placement.Rotation.Axis.y = VThreadProfile027.Placement.Rotation.Axis.y
  expr: .Placement.Rotation.Axis.x = VThreadProfile027.Placement.Rotation.Axis.x
  expr: .Placement.Rotation.Angle = VThreadProfile027.Placement.Rotation.Angle
  expr: .Placement.Base.z = VThreadProfile027.Placement.Base.z
  expr: .Placement.Base.y = VThreadProfile027.Placement.Base.y
  expr: .Placement.Base.x = VThreadProfile027.Placement.Base.x
  expr: Height = VThreadProfile027.ThreadCount * VThreadProfile027.Pitch
  expr: Pitch = VThreadProfile027.Pitch
FEATURE [PartDesign::ShapeBinder] ShapeBinder028
  Placement = pos=(-4,-5,8.5) rot=(0,0,1;2e-06rad)
  Support = -> [Helix032]
  TraceSupport = false
FEATURE [PartDesign::SubtractivePipe] SubtractivePipe021
  AuxilleryCurvelinear = true
  AuxillerySpineTangent = false
  BaseFeature = -> SubtractivePipe020
  Binormal = (0,0,0)
  Mode = 2
  Placement = pos=(0,0,18.5) rot=(0,1,0;3.14159rad)
  Profile = -> VThreadProfile027
  Spine = -> ShapeBinder028
  SpineTangent = false
  Transformation = 0
  Transition = 0
FEATURE [Sketcher::SketchObject] Sketch031
  FullyConstrained = true
  MapMode = 5
  Placement = pos=(-3.7e-15,0,8.5) rot=(0,1,0;3.14159rad)
  Support = -> [DatumPlane007]
  sketch-geometry (2):
    g0: Circle CenterX=-8 CenterY=0 CenterZ=0 NormalX=0 NormalY=0 NormalZ=1 AngleXU=0 Radius=1.5
    g1: Circle CenterX=8 CenterY=0 CenterZ=0 NormalX=0 NormalY=0 NormalZ=1 AngleXU=0 Radius=1.5
  constraints (5):
    c: PointOnObject(g0,g-1)
    c: Equal(g1,g0)
    c: Radius(g1) = 1.5
    c: Symmetric(g0,g1,g-1)
    c: Distance(g1,g0) = 16
FEATURE [PartDesign::Pocket] Pocket040
  BaseFeature = -> SubtractivePipe021
  Length = 6
  Length2 = 100
  Placement = pos=(0,0,18.5) rot=(0,1,0;3.14159rad)
  Profile = -> Sketch031
  Type = 0
FEATURE [PartDesign::Body] Body002  label="heatblock"
  Group = -> [DatumPlane004,Sketch004,Pad,DatumPlane005,Sketch005,Pocket002,DatumPlane006,Sketch006,Pocket006,DatumPlane007,Sketch007,Pocket007,Sketch008,Pocket008,Pocket038,Pocket039,VThreadProfile024,ShapeBinder025,SubtractivePipe,VThreadProfile025,ShapeBinder026,SubtractivePipe019,VThreadProfile026,ShapeBinder027,SubtractivePipe020,VThreadProfile027,ShapeBinder028,SubtractivePipe021,Sketch031,Pocket040]
  Origin = -> Origin003
  Tip = -> Pocket040
FEATURE [App::Part] Part  label="red lizard hotend"
  Group = -> [Body,Body001,Body002,Body003,Body004,Body005,Body006,Body007,Body009,Body008,Body011,Helix032,Helix030,Helix028,Helix027,Helix025,Helix023,Helix024,Helix017,Helix022,Helix031,Helix001,Helix016,Helix014,Helix026,Helix021,Helix029,Helix,Helix002,Helix015]
  Id = i4
  Origin = -> Origin
